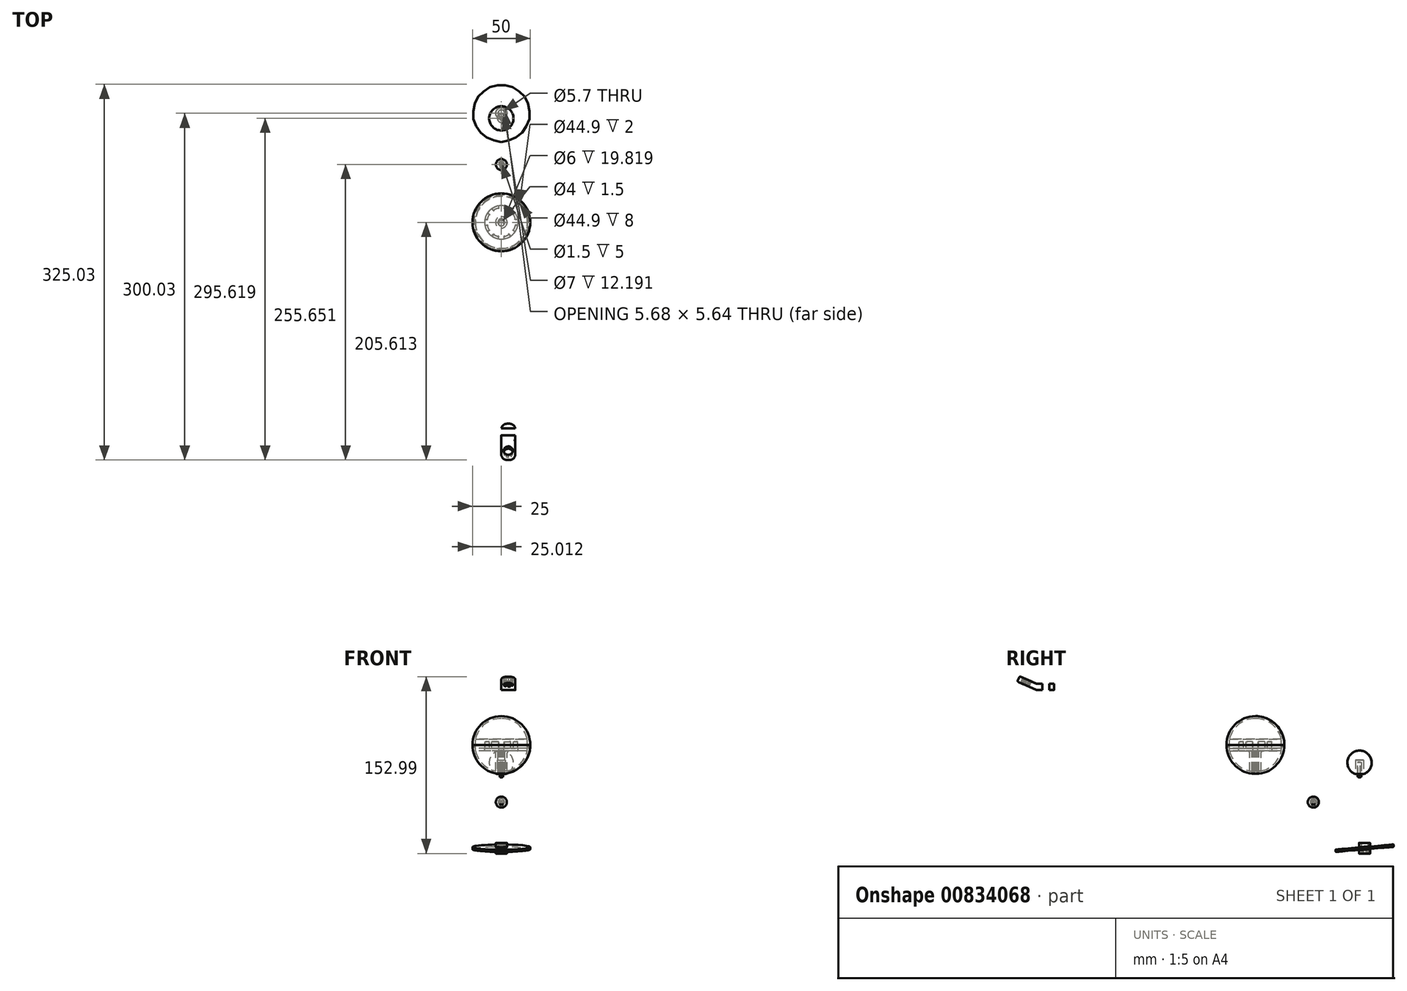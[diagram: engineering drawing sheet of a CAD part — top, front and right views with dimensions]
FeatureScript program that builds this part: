
annotation { "Feature Type Name" : "Feature", "Feature Type Description" : "" }
export const myFeature = defineFeature(function(context is Context, id is Id, definition is map)
    precondition{}
    {
        {
            var Q0;
            Q0=qCreatedBy(makeId("Right.planeOp"),FACE);
            var sketch = newSketch(context, id + "F0", { "sketchPlane" : qUnion([Q0])});
            skLineSegment(sketch, "E0", {"start": v(-206.61, 164.55) * mm, "end": v(-191.94, 158.17) * mm});
            skLineSegment(sketch, "E1", {"start": v(-191.94, 158.17) * mm, "end": v(-175.94, 158.17) * mm});
            skLineSegment(sketch, "E2", {"start": v(-206.61, 164.55) * mm, "end": v(-208.6, 159.96) * mm});
            skLineSegment(sketch, "E3", {"start": v(-208.6, 159.96) * mm, "end": v(-191.94, 152.71) * mm});
            skLineSegment(sketch, "E4", {"start": v(-191.94, 152.71) * mm, "end": v(-175.94, 152.71) * mm});
            skLineSegment(sketch, "E5", {"start": v(-175.94, 152.71) * mm, "end": v(-175.94, 158.17) * mm});
            skLineSegment(sketch, "E6.bottom", {"start": v(-186.94, 158.17) * mm, "end": v(-180.94, 158.17) * mm});
            skLineSegment(sketch, "E6.top", {"start": v(-186.94, 152.71) * mm, "end": v(-180.94, 152.71) * mm});
            skLineSegment(sketch, "E6.left", {"start": v(-186.94, 158.17) * mm, "end": v(-186.94, 152.71) * mm});
            skLineSegment(sketch, "E6.right", {"start": v(-180.94, 158.17) * mm, "end": v(-180.94, 152.71) * mm});
            skLineSegment(sketch, "E7", {"start": v(-202.94, 162.95) * mm, "end": v(-204.94, 158.37) * mm});
            skLineSegment(sketch, "E8", {"start": v(-195.6, 159.76) * mm, "end": v(-197.6, 155.18) * mm});
            skLineSegment(sketch, "E9", {"start": v(-199.28, 161.36) * mm, "end": v(-203.57, 151.48) * mm});
            skLineSegment(sketch, "E10", {"start": v(-199.28, 161.36) * mm, "end": v(-184, 196.48) * mm});
            skLineSegment(sketch, "E11", {"start": v(-183.94, 158.17) * mm, "end": v(-183.94, 142.94) * mm});
            skLineSegment(sketch, "E12", {"start": v(-183.94, 158.17) * mm, "end": v(-183.94, 196.54) * mm});
            skLineSegment(sketch, "E13", {"start": v(-200.94, 172.57) * mm, "end": v(-189.94, 167.78) * mm});
            skLineSegment(sketch, "E14", {"start": v(-189.94, 167.78) * mm, "end": v(-177.94, 167.78) * mm});
            skLineSegment(sketch, "E15", {"start": v(-298.35, 148.72) * mm, "end": v(-283.68, 142.34) * mm});
            skLineSegment(sketch, "E16", {"start": v(-283.68, 142.34) * mm, "end": v(-268.68, 142.34) * mm});
            skLineSegment(sketch, "E17", {"start": v(-298.35, 148.72) * mm, "end": v(-300.34, 144.14) * mm});
            skLineSegment(sketch, "E18", {"start": v(-300.34, 144.14) * mm, "end": v(-283.68, 136.9) * mm});
            skLineSegment(sketch, "E19", {"start": v(-283.68, 136.9) * mm, "end": v(-268.68, 136.9) * mm});
            skLineSegment(sketch, "E20", {"start": v(-268.68, 136.9) * mm, "end": v(-268.68, 142.34) * mm});
            skLineSegment(sketch, "E21.bottom", {"start": v(-278.68, 142.34) * mm, "end": v(-272.68, 142.34) * mm});
            skLineSegment(sketch, "E21.top", {"start": v(-278.68, 136.9) * mm, "end": v(-272.68, 136.9) * mm});
            skLineSegment(sketch, "E21.left", {"start": v(-278.68, 142.34) * mm, "end": v(-278.68, 136.9) * mm});
            skLineSegment(sketch, "E21.right", {"start": v(-272.68, 142.34) * mm, "end": v(-272.68, 136.9) * mm});
            skLineSegment(sketch, "E22", {"start": v(-294.68, 147.13) * mm, "end": v(-296.68, 142.54) * mm});
            skLineSegment(sketch, "E23", {"start": v(-287.35, 143.94) * mm, "end": v(-289.34, 139.35) * mm});
            skSolve(sketch);
        }
        {
            var Q0;
            {var subQ0=sQuery(id+"F0.wireOp",EDGE,"E17");Q0=makeQuery(id+"F0.imprint","IMPRINT",FACE,{"disambiguationData":[TD([[makeQuery(id+"F0.imprint","IMPRINT",EDGE,{"derivedFrom":subQ0}),1.0]])]});}
            var Q1;
            {var subQ3=sQuery(id+"F0.wireOp",EDGE,"E21.left");Q1=makeQuery(id+"F0.imprint","IMPRINT",FACE,{"disambiguationData":[TD([[makeQuery(id+"F0.imprint","IMPRINT",EDGE,{"derivedFrom":subQ3}),-1.0]])]});}
            var Q2;
            {var subQ0=sQuery(id+"F0.wireOp",EDGE,"E22");Q2=makeQuery(id+"F0.imprint","IMPRINT",FACE,{"disambiguationData":[TD([[makeQuery(id+"F0.imprint","IMPRINT",EDGE,{"derivedFrom":subQ0}),1.0]])]});}
            var Q3;
            Q3=makeQuery(id+"F0.imprint","IMPRINT",FACE,{"disambiguationData":[TD([[makeQuery(id+"F0.imprint","IMPRINT",EDGE,{"derivedFrom":sQuery(id+"F0.wireOp",EDGE,"E21.bottom")}),-1.0]])]});
            var Q4;
            {var subQ0=sQuery(id+"F0.wireOp",EDGE,"E20");Q4=makeQuery(id+"F0.imprint","IMPRINT",FACE,{"disambiguationData":[TD([[makeQuery(id+"F0.imprint","IMPRINT",EDGE,{"derivedFrom":subQ0}),1.0]])]});}
            extrude(context, id + "F1", {"entities" : qUnion([Q0, Q1, Q2, Q3, Q4]), "depth" : 12 * mm, "offsetDistance" : 25 * mm});
        }
        {
            var Q0;
            Q0=makeQuery(id+"F1.opExtrude","SWEPT_FACE",FACE,{"disambiguationData":[OSD([sQuery(id+"F0.wireOp",EDGE,"E15")])]});
            var sketch = newSketch(context, id + "F2", { "sketchPlane" : qUnion([Q0])});
            skArc(sketch, "E24", {"start": v(7.7, -322.29) * mm, "mid": v(6.7, -321.97) * mm, "end": v(5.66, -321.92) * mm});
            skArc(sketch, "E25", {"start": v(9.2, -323.68) * mm, "mid": v(8.52, -322.93) * mm, "end": v(7.66, -322.38) * mm});
            skLineSegment(sketch, "E26", {"start": v(7.66, -322.38) * mm, "end": v(7.7, -322.29) * mm});
            skLineSegment(sketch, "E27", {"start": v(9.2, -323.68) * mm, "end": v(9.28, -323.62) * mm});
            skArc(sketch, "E28.1.0", {"start": v(5.67, -322.02) * mm, "mid": v(4.68, -322.24) * mm, "end": v(3.77, -322.7) * mm});
            skLineSegment(sketch, "E28.1.1", {"start": v(3.77, -322.7) * mm, "end": v(3.71, -322.63) * mm});
            skLineSegment(sketch, "E28.1.2", {"start": v(5.67, -322.02) * mm, "end": v(5.66, -321.92) * mm});
            skArc(sketch, "E28.2.0", {"start": v(2.47, -324.25) * mm, "mid": v(2.16, -325.22) * mm, "end": v(2.11, -326.24) * mm});
            skLineSegment(sketch, "E28.2.1", {"start": v(2.11, -326.24) * mm, "end": v(2.01, -326.25) * mm});
            skLineSegment(sketch, "E28.2.2", {"start": v(2.47, -324.25) * mm, "end": v(2.38, -324.2) * mm});
            skArc(sketch, "E28.3.0", {"start": v(2.8, -328.14) * mm, "mid": v(3.48, -328.89) * mm, "end": v(4.34, -329.44) * mm});
            skLineSegment(sketch, "E28.3.1", {"start": v(4.34, -329.44) * mm, "end": v(4.3, -329.53) * mm});
            skLineSegment(sketch, "E28.3.2", {"start": v(2.8, -328.14) * mm, "end": v(2.72, -328.2) * mm});
            skArc(sketch, "E28.4.0", {"start": v(6.33, -329.8) * mm, "mid": v(7.32, -329.58) * mm, "end": v(8.23, -329.1) * mm});
            skLineSegment(sketch, "E28.4.1", {"start": v(8.23, -329.1) * mm, "end": v(8.29, -329.2) * mm});
            skLineSegment(sketch, "E28.4.2", {"start": v(6.33, -329.8) * mm, "end": v(6.34, -329.9) * mm});
            skArc(sketch, "E28.5.0", {"start": v(9.53, -327.57) * mm, "mid": v(9.84, -326.6) * mm, "end": v(9.89, -325.58) * mm});
            skLineSegment(sketch, "E28.5.1", {"start": v(9.89, -325.58) * mm, "end": v(9.99, -325.57) * mm});
            skLineSegment(sketch, "E28.5.2", {"start": v(9.53, -327.57) * mm, "end": v(9.62, -327.6) * mm});
            skArc(sketch, "E29.trimOffspring", {"start": v(3.71, -322.63) * mm, "mid": v(2.94, -323.33) * mm, "end": v(2.38, -324.2) * mm});
            skArc(sketch, "E30.trimOffspring", {"start": v(2.01, -326.25) * mm, "mid": v(2.24, -327.27) * mm, "end": v(2.72, -328.2) * mm});
            skArc(sketch, "E31.trimOffspring", {"start": v(9.99, -325.57) * mm, "mid": v(9.76, -324.55) * mm, "end": v(9.28, -323.62) * mm});
            skArc(sketch, "E32.trimOffspring", {"start": v(8.29, -329.2) * mm, "mid": v(9.06, -328.49) * mm, "end": v(9.62, -327.6) * mm});
            skArc(sketch, "E33.trimOffspring", {"start": v(4.3, -329.53) * mm, "mid": v(5.3, -329.85) * mm, "end": v(6.34, -329.9) * mm});
            skSolve(sketch);
        }
        {
            var Q0;
            Q0=makeQuery(id+"F1.opExtrude","SWEPT_FACE",FACE,{"disambiguationData":[OSD([sQuery(id+"F0.wireOp",EDGE,"E16"),sQuery(id+"F0.wireOp",EDGE,"E21.bottom")])]});
            var sketch = newSketch(context, id + "F3", { "sketchPlane" : qUnion([Q0])});
            skArc(sketch, "E34", {"start": v(7.34, -273) * mm, "mid": v(6.6, -272.74) * mm, "end": v(5.81, -272.68) * mm});
            skArc(sketch, "E35", {"start": v(8.38, -274.1) * mm, "mid": v(7.89, -273.54) * mm, "end": v(7.27, -273.13) * mm});
            skLineSegment(sketch, "E36", {"start": v(7.27, -273.13) * mm, "end": v(7.34, -273) * mm});
            skLineSegment(sketch, "E37", {"start": v(8.38, -274.1) * mm, "end": v(8.5, -274.02) * mm});
            skLineSegment(sketch, "E38.1.0", {"start": v(4.43, -273.3) * mm, "end": v(4.34, -273.18) * mm});
            skArc(sketch, "E38.1.1", {"start": v(5.82, -272.83) * mm, "mid": v(5.1, -272.98) * mm, "end": v(4.43, -273.3) * mm});
            skLineSegment(sketch, "E38.1.2", {"start": v(5.82, -272.83) * mm, "end": v(5.81, -272.68) * mm});
            skLineSegment(sketch, "E38.2.0", {"start": v(3.16, -275.85) * mm, "end": v(3, -275.86) * mm});
            skArc(sketch, "E38.2.1", {"start": v(3.45, -274.4) * mm, "mid": v(3.2, -275.11) * mm, "end": v(3.16, -275.85) * mm});
            skLineSegment(sketch, "E38.2.2", {"start": v(3.45, -274.4) * mm, "end": v(3.31, -274.34) * mm});
            skLineSegment(sketch, "E38.3.0", {"start": v(4.73, -278.23) * mm, "end": v(4.66, -278.36) * mm});
            skArc(sketch, "E38.3.1", {"start": v(3.62, -277.25) * mm, "mid": v(4.11, -277.81) * mm, "end": v(4.73, -278.23) * mm});
            skLineSegment(sketch, "E38.3.2", {"start": v(3.62, -277.25) * mm, "end": v(3.5, -277.33) * mm});
            skLineSegment(sketch, "E38.4.0", {"start": v(7.57, -278.05) * mm, "end": v(7.66, -278.18) * mm});
            skArc(sketch, "E38.4.1", {"start": v(6.18, -278.52) * mm, "mid": v(6.9, -278.38) * mm, "end": v(7.57, -278.05) * mm});
            skLineSegment(sketch, "E38.4.2", {"start": v(6.18, -278.52) * mm, "end": v(6.19, -278.67) * mm});
            skLineSegment(sketch, "E38.5.0", {"start": v(8.84, -275.5) * mm, "end": v(9, -275.5) * mm});
            skArc(sketch, "E38.5.1", {"start": v(8.55, -276.95) * mm, "mid": v(8.8, -276.24) * mm, "end": v(8.84, -275.5) * mm});
            skLineSegment(sketch, "E38.5.2", {"start": v(8.55, -276.95) * mm, "end": v(8.69, -277.01) * mm});
            skArc(sketch, "E39.trimOffspring", {"start": v(4.34, -273.18) * mm, "mid": v(3.75, -273.7) * mm, "end": v(3.31, -274.34) * mm});
            skArc(sketch, "E40.trimOffspring", {"start": v(3, -275.86) * mm, "mid": v(3.16, -276.63) * mm, "end": v(3.5, -277.33) * mm});
            skArc(sketch, "E41.trimOffspring", {"start": v(4.66, -278.36) * mm, "mid": v(5.4, -278.62) * mm, "end": v(6.19, -278.67) * mm});
            skArc(sketch, "E42.trimOffspring", {"start": v(7.66, -278.18) * mm, "mid": v(8.25, -277.66) * mm, "end": v(8.69, -277.01) * mm});
            skArc(sketch, "E43.trimOffspring", {"start": v(9, -275.5) * mm, "mid": v(8.84, -274.72) * mm, "end": v(8.5, -274.02) * mm});
            skSolve(sketch);
        }
        {
            var Q0;
            Q0=makeQuery(id+"F2.imprint","IMPRINT",FACE,{"disambiguationData":[TD([[makeQuery(id+"F2.imprint","IMPRINT",EDGE,{"derivedFrom":sQuery(id+"F2.wireOp",EDGE,"E24")}),1.0]])]});
            extrude(context, id + "F4", {"entities" : qUnion([Q0]), "operationType" : NewBodyOperationType.REMOVE, "oppositeDirection" : true, "depth" : 25 * mm, "offsetDistance" : 25 * mm});
        }
        {
            var Q0;
            Q0=makeQuery(id+"F3.imprint","IMPRINT",FACE,{"disambiguationData":[TD([[makeQuery(id+"F3.imprint","IMPRINT",EDGE,{"derivedFrom":sQuery(id+"F3.wireOp",EDGE,"E34")}),1.0]])]});
            extrude(context, id + "F5", {"entities" : qUnion([Q0]), "operationType" : NewBodyOperationType.REMOVE, "oppositeDirection" : true, "depth" : 25 * mm, "offsetDistance" : 25 * mm});
        }
        {
            var Q0;
            Q0=makeQuery(id+"F1.opExtrude","CAP_EDGE",EDGE,{"disambiguationData":[OSD([sQuery(id+"F0.wireOp",EDGE,"E17")])],"isStart":false});
            var Q1;
            Q1=makeQuery(id+"F1.opExtrude","CAP_EDGE",EDGE,{"disambiguationData":[OSD([sQuery(id+"F0.wireOp",EDGE,"E17")])],"isStart":true});
            var Q2;
            Q2=makeQuery(id+"F1.opExtrude","CAP_EDGE",EDGE,{"disambiguationData":[OSD([sQuery(id+"F0.wireOp",EDGE,"E20")])],"isStart":false});
            var Q3;
            Q3=makeQuery(id+"F1.opExtrude","CAP_EDGE",EDGE,{"disambiguationData":[OSD([sQuery(id+"F0.wireOp",EDGE,"E20")])],"isStart":true});
            fillet(context, id + "F6", {"entities" : qUnion([Q0, Q1, Q2, Q3]), "radius" : 5 * mm, "tangentPropagation" : true, "allowEdgeOverflow" : false});
        }
        {
            var Q0;
            Q0=makeQuery(id+"F1.opExtrude","CAP_EDGE",EDGE,{"disambiguationData":[OSD([sQuery(id+"F0.wireOp",EDGE,"E15")])],"isStart":false});
            var Q1;
            Q1=makeQuery(id+"F6.opFillet","BLEND_EDGE",EDGE,{"blendedFrom":[makeQuery(id+"F1.opExtrude","CAP_EDGE",EDGE,{"disambiguationData":[OSD([sQuery(id+"F0.wireOp",EDGE,"E17")])],"isStart":false}),makeQuery(id+"F1.opExtrude","SWEPT_FACE",FACE,{"disambiguationData":[OSD([sQuery(id+"F0.wireOp",EDGE,"E15")])]})],"blendedInto":[makeQuery(id+"F1.opExtrude","SWEPT_FACE",FACE,{"disambiguationData":[OSD([sQuery(id+"F0.wireOp",EDGE,"E15")])]})]});
            var Q2;
            Q2=makeQuery(id+"F1.opExtrude","CAP_EDGE",EDGE,{"disambiguationData":[OSD([sQuery(id+"F0.wireOp",EDGE,"E16"),sQuery(id+"F0.wireOp",EDGE,"E21.bottom")])],"isStart":true});
            var Q3;
            Q3=makeQuery(id+"F1.opExtrude","CAP_EDGE",EDGE,{"disambiguationData":[OSD([sQuery(id+"F0.wireOp",EDGE,"E18")])],"isStart":false});
            var Q4;
            Q4=makeQuery(id+"F1.opExtrude","CAP_EDGE",EDGE,{"disambiguationData":[OSD([sQuery(id+"F0.wireOp",EDGE,"E19"),sQuery(id+"F0.wireOp",EDGE,"E21.top")])],"isStart":true});
            var Q5;
            Q5=makeQuery(id+"F1.opExtrude","SWEPT_EDGE",EDGE,{"disambiguationData":[OSD([sQuery(id+"F0.wireOp",EDGE,"E18"),sQuery(id+"F0.wireOp",EDGE,"E19")])]});
            var Q6;
            Q6=makeQuery(id+"F1.opExtrude","SWEPT_EDGE",EDGE,{"disambiguationData":[OSD([sQuery(id+"F0.wireOp",EDGE,"E15"),sQuery(id+"F0.wireOp",EDGE,"E16")])]});
            fillet(context, id + "F7", {"entities" : qUnion([Q0, Q1, Q2, Q3, Q4, Q5, Q6]), "radius" : 1 * mm, "tangentPropagation" : true, "allowEdgeOverflow" : false});
        }
        {
            var Q0;
            Q0=qCreatedBy(makeId("Right.planeOp"),FACE);
            var sketch = newSketch(context, id + "F8", { "sketchPlane" : qUnion([Q0])});
            skArc(sketch, "E44", {"start": v(-94.42, 114.27) * mm, "mid": v(-119.37, 90.78) * mm, "end": v(-97.42, 64.45) * mm});
            skLineSegment(sketch, "E45.right", {"start": v(-97.42, 64.45) * mm, "end": v(-97.42, 84.27) * mm});
            skPoint(sketch, "E46.orphan", {"position": v(-97.42, 61.17) * mm});
            skPoint(sketch, "E47.orphan", {"position": v(-91.42, 61.17) * mm});
            skPoint(sketch, "E48.left.end.orphan", {"position": v(-71.97, 94.27) * mm});
            skPoint(sketch, "E49.orphan", {"position": v(-91.42, 117.38) * mm});
            skPoint(sketch, "E50.orphan", {"position": v(-97.42, 117.38) * mm});
            skPoint(sketch, "E48.right.end.orphan", {"position": v(-116.87, 94.27) * mm});
            skPoint(sketch, "E48.right.start.orphan", {"position": v(-116.87, 84.27) * mm});
            skLineSegment(sketch, "E51", {"start": v(-96.92, 86.27) * mm, "end": v(-106.37, 86.27) * mm});
            skLineSegment(sketch, "E52", {"start": v(-96.42, 85.77) * mm, "end": v(-96.42, 84.27) * mm});
            skLineSegment(sketch, "E53", {"start": v(-108.37, 84.27) * mm, "end": v(-101.42, 84.27) * mm});
            skLineSegment(sketch, "E54", {"start": v(-99.42, 82.27) * mm, "end": v(-99.42, 66.82) * mm});
            skLineSegment(sketch, "E55.top", {"start": v(-108.87, 92.27) * mm, "end": v(-106.87, 92.27) * mm});
            skLineSegment(sketch, "E55.left", {"start": v(-108.87, 86.27) * mm, "end": v(-108.87, 92.27) * mm});
            skLineSegment(sketch, "E55.right", {"start": v(-106.87, 86.77) * mm, "end": v(-106.87, 92.27) * mm});
            skArc(sketch, "E56.trimOffspring", {"start": v(-116.87, 84.27) * mm, "mid": v(-110.68, 73) * mm, "end": v(-99.42, 66.82) * mm});
            skLineSegment(sketch, "E57.trimOffspring", {"start": v(-116.87, 86.27) * mm, "end": v(-117.22, 86.27) * mm});
            skLineSegment(sketch, "E58.trimOffspring", {"start": v(-96.42, 84.27) * mm, "end": v(-97.42, 84.27) * mm});
            skLineSegment(sketch, "E59", {"start": v(-116.87, 94.27) * mm, "end": v(-116.87, 86.27) * mm});
            skLineSegment(sketch, "E60", {"start": v(-119.42, 89.27) * mm, "end": v(-118.14, 89.27) * mm});
            skPoint(sketch, "E60.startSnap0", {"position": v(-116.87, 89.27) * mm});
            skLineSegment(sketch, "E61", {"start": v(-118.14, 89.27) * mm, "end": v(-117.22, 86.27) * mm});
            skLineSegment(sketch, "E62", {"start": v(-94.42, 112.27) * mm, "end": v(-94.42, 114.27) * mm});
            skArc(sketch, "E63.trimOffspring", {"start": v(-94.42, 112.27) * mm, "mid": v(-108.8, 107.22) * mm, "end": v(-116.87, 94.27) * mm});
            skPoint(sketch, "E48.bottom.start.orphan", {"position": v(-71.97, 84.27) * mm});
            skLineSegment(sketch, "E64", {"start": v(-94.42, 89.27) * mm, "end": v(-94.42, 76.17) * mm});
            skLineSegment(sketch, "E65", {"start": v(-108.87, 86.27) * mm, "end": v(-108.87, 84.77) * mm});
            skLineSegment(sketch, "E66", {"start": v(-116.87, 84.27) * mm, "end": v(-116.87, 86.27) * mm});
            skPoint(sketch, "E67.visualSharp", {"position": v(-106.87, 86.27) * mm});
            skArc(sketch, "E67.filletArc", {"start": v(-106.87, 86.77) * mm, "mid": v(-106.72, 86.42) * mm, "end": v(-106.37, 86.27) * mm});
            skPoint(sketch, "E68.visualSharp", {"position": v(-108.87, 84.27) * mm});
            skArc(sketch, "E68.filletArc", {"start": v(-108.87, 84.77) * mm, "mid": v(-108.72, 84.42) * mm, "end": v(-108.37, 84.27) * mm});
            skPoint(sketch, "E69.visualSharp", {"position": v(-99.42, 84.27) * mm});
            skArc(sketch, "E69.filletArc", {"start": v(-99.42, 82.27) * mm, "mid": v(-100, 83.69) * mm, "end": v(-101.42, 84.27) * mm});
            skPoint(sketch, "E70.visualSharp", {"position": v(-96.42, 86.27) * mm});
            skArc(sketch, "E70.filletArc", {"start": v(-96.42, 85.77) * mm, "mid": v(-96.56, 86.13) * mm, "end": v(-96.92, 86.27) * mm});
            skSolve(sketch);
        }
        {
            var Q0;
            {var subQ1=sQuery(id+"F8.wireOp",EDGE,"E45.right");Q0=makeQuery(id+"F8.imprint","IMPRINT",FACE,{"disambiguationData":[TD([[makeQuery(id+"F8.imprint","IMPRINT",EDGE,{"derivedFrom":subQ1}),1.0]])]});}
            var Q1;
            Q1=sQuery(id+"F8.wireOp",EDGE,"E64");
            revolve(context, id + "F9", {"surfaceOperationType" : NewSurfaceOperationType.NEW, "entities" : qUnion([Q0]), "axis" : qUnion([Q1]), "revolveType" : RevolveType.FULL});
        }
        {
            var Q0;
            {var subQ0=sQuery(id+"F8.wireOp",EDGE,"E59");Q0=makeQuery(id+"F8.imprint","IMPRINT",FACE,{"disambiguationData":[TD([[makeQuery(id+"F8.imprint","IMPRINT",EDGE,{"derivedFrom":subQ0}),-1.0]])]});}
            var Q1;
            Q1=sQuery(id+"F8.wireOp",EDGE,"E64");
            revolve(context, id + "F10", {"surfaceOperationType" : NewSurfaceOperationType.NEW, "entities" : qUnion([Q0]), "axis" : qUnion([Q1]), "revolveType" : RevolveType.FULL});
        }
        {
            var Q0;
            Q0=makeQuery(id+"F9.opRevolve","SWEPT_FACE",FACE,{"disambiguationData":[OSD([sQuery(id+"F8.wireOp",EDGE,"E55.top")])]});
            var sketch = newSketch(context, id + "F11", { "sketchPlane" : qUnion([Q0])});
            skArc(sketch, "E71", {"start": v(2.4, -79.89) * mm, "mid": v(0, -79.7) * mm, "end": v(-2.4, -79.89) * mm});
            skArc(sketch, "E72", {"start": v(2.4, -83.2) * mm, "mid": v(0, -82.95) * mm, "end": v(-2.4, -83.2) * mm});
            skLineSegment(sketch, "E73", {"start": v(-2.4, -79.89) * mm, "end": v(-2.4, -83.2) * mm});
            skLineSegment(sketch, "E74", {"start": v(2.4, -79.89) * mm, "end": v(2.4, -83.2) * mm});
            skArc(sketch, "E75.1.0", {"start": v(-8.58, -82.45) * mm, "mid": v(-10.41, -84) * mm, "end": v(-11.97, -85.84) * mm});
            skLineSegment(sketch, "E75.1.1", {"start": v(-8.58, -82.45) * mm, "end": v(-6.24, -84.79) * mm});
            skLineSegment(sketch, "E75.1.2", {"start": v(-11.97, -85.84) * mm, "end": v(-9.63, -88.18) * mm});
            skArc(sketch, "E75.1.3", {"start": v(-6.24, -84.79) * mm, "mid": v(-8.11, -86.3) * mm, "end": v(-9.63, -88.18) * mm});
            skArc(sketch, "E75.2.0", {"start": v(-14.53, -92.02) * mm, "mid": v(-14.73, -94.42) * mm, "end": v(-14.53, -96.82) * mm});
            skLineSegment(sketch, "E75.2.1", {"start": v(-14.53, -92.02) * mm, "end": v(-11.22, -92.02) * mm});
            skLineSegment(sketch, "E75.2.2", {"start": v(-14.53, -96.82) * mm, "end": v(-11.22, -96.82) * mm});
            skArc(sketch, "E75.2.3", {"start": v(-11.22, -92.02) * mm, "mid": v(-11.47, -94.42) * mm, "end": v(-11.22, -96.82) * mm});
            skArc(sketch, "E75.3.0", {"start": v(-11.97, -103) * mm, "mid": v(-10.41, -104.83) * mm, "end": v(-8.58, -106.39) * mm});
            skLineSegment(sketch, "E75.3.1", {"start": v(-11.97, -103) * mm, "end": v(-9.63, -100.65) * mm});
            skLineSegment(sketch, "E75.3.2", {"start": v(-8.58, -106.39) * mm, "end": v(-6.24, -104.05) * mm});
            skArc(sketch, "E75.3.3", {"start": v(-9.63, -100.65) * mm, "mid": v(-8.11, -102.53) * mm, "end": v(-6.24, -104.05) * mm});
            skArc(sketch, "E75.4.0", {"start": v(-2.4, -108.95) * mm, "mid": v(0, -109.14) * mm, "end": v(2.4, -108.95) * mm});
            skLineSegment(sketch, "E75.4.1", {"start": v(-2.4, -108.95) * mm, "end": v(-2.4, -105.64) * mm});
            skLineSegment(sketch, "E75.4.2", {"start": v(2.4, -108.95) * mm, "end": v(2.4, -105.64) * mm});
            skArc(sketch, "E75.4.3", {"start": v(-2.4, -105.64) * mm, "mid": v(0, -105.89) * mm, "end": v(2.4, -105.64) * mm});
            skArc(sketch, "E75.5.0", {"start": v(8.58, -106.39) * mm, "mid": v(10.41, -104.83) * mm, "end": v(11.97, -103) * mm});
            skLineSegment(sketch, "E75.5.1", {"start": v(8.58, -106.39) * mm, "end": v(6.24, -104.05) * mm});
            skLineSegment(sketch, "E75.5.2", {"start": v(11.97, -103) * mm, "end": v(9.63, -100.65) * mm});
            skArc(sketch, "E75.5.3", {"start": v(6.24, -104.05) * mm, "mid": v(8.11, -102.53) * mm, "end": v(9.63, -100.65) * mm});
            skArc(sketch, "E75.6.0", {"start": v(14.53, -96.82) * mm, "mid": v(14.73, -94.42) * mm, "end": v(14.53, -92.02) * mm});
            skLineSegment(sketch, "E75.6.1", {"start": v(14.53, -96.82) * mm, "end": v(11.22, -96.82) * mm});
            skLineSegment(sketch, "E75.6.2", {"start": v(14.53, -92.02) * mm, "end": v(11.22, -92.02) * mm});
            skArc(sketch, "E75.6.3", {"start": v(11.22, -96.82) * mm, "mid": v(11.47, -94.42) * mm, "end": v(11.22, -92.02) * mm});
            skArc(sketch, "E75.7.0", {"start": v(11.97, -85.84) * mm, "mid": v(10.41, -84) * mm, "end": v(8.58, -82.45) * mm});
            skLineSegment(sketch, "E75.7.1", {"start": v(11.97, -85.84) * mm, "end": v(9.63, -88.18) * mm});
            skLineSegment(sketch, "E75.7.2", {"start": v(8.58, -82.45) * mm, "end": v(6.24, -84.79) * mm});
            skArc(sketch, "E75.7.3", {"start": v(9.63, -88.18) * mm, "mid": v(8.11, -86.3) * mm, "end": v(6.24, -84.79) * mm});
            skSolve(sketch);
        }
        {
            var Q0;
            Q0 = qSketchRegion(id + "F11", true);
            extrude(context, id + "F12", {"entities" : qUnion([Q0]), "operationType" : NewBodyOperationType.REMOVE, "oppositeDirection" : true, "depth" : 6 * mm, "offsetDistance" : 25 * mm});
        }
        {
            var Q0;
            {var subQ0=sQuery(id+"F8.wireOp",EDGE,"E55.top");var subQ1=sQuery(id+"F8.wireOp",EDGE,"E55.left");Q0=makeQuery(id+"F12.boolean.opBoolean","SPLIT",EDGE,{"disambiguationData":[TD([makeQuery(id+"F12.opExtrude","SWEPT_FACE",FACE,{"disambiguationData":[OSD([sQuery(id+"F11.wireOp",EDGE,"E75.3.2")])]})])],"derivedFrom":makeQuery(id+"F9.opRevolve","SWEPT_EDGE",EDGE,{"disambiguationData":[OSD([subQ0,subQ1])]})});}
            var Q1;
            Q1=makeQuery(id+"F12.boolean.opBoolean","COPY",EDGE,{"derivedFrom":makeQuery(id+"F12.opExtrude","CAP_EDGE",EDGE,{"disambiguationData":[OSD([sQuery(id+"F11.wireOp",EDGE,"E75.4.1")])],"isStart":true})});
            var Q2;
            {var subQ0=sQuery(id+"F8.wireOp",EDGE,"E55.top");var subQ1=sQuery(id+"F8.wireOp",EDGE,"E55.right");Q2=makeQuery(id+"F12.boolean.opBoolean","SPLIT",EDGE,{"disambiguationData":[TD([makeQuery(id+"F12.opExtrude","SWEPT_FACE",FACE,{"disambiguationData":[OSD([sQuery(id+"F11.wireOp",EDGE,"E75.3.2")])]})])],"derivedFrom":makeQuery(id+"F9.opRevolve","SWEPT_EDGE",EDGE,{"disambiguationData":[OSD([subQ0,subQ1])]})});}
            var Q3;
            Q3=makeQuery(id+"F12.boolean.opBoolean","COPY",EDGE,{"derivedFrom":makeQuery(id+"F12.opExtrude","CAP_EDGE",EDGE,{"disambiguationData":[OSD([sQuery(id+"F11.wireOp",EDGE,"E75.3.2")])],"isStart":true})});
            var Q4;
            Q4=makeQuery(id+"F12.boolean.opBoolean","COPY",EDGE,{"derivedFrom":makeQuery(id+"F12.opExtrude","CAP_EDGE",EDGE,{"disambiguationData":[OSD([sQuery(id+"F11.wireOp",EDGE,"E75.3.1")])],"isStart":true})});
            var Q5;
            {var subQ0=sQuery(id+"F8.wireOp",EDGE,"E55.top");var subQ1=sQuery(id+"F8.wireOp",EDGE,"E55.left");Q5=makeQuery(id+"F12.boolean.opBoolean","SPLIT",EDGE,{"disambiguationData":[TD([makeQuery(id+"F12.opExtrude","SWEPT_FACE",FACE,{"disambiguationData":[OSD([sQuery(id+"F11.wireOp",EDGE,"E75.2.2")])]})])],"derivedFrom":makeQuery(id+"F9.opRevolve","SWEPT_EDGE",EDGE,{"disambiguationData":[OSD([subQ0,subQ1])]})});}
            var Q6;
            {var subQ0=sQuery(id+"F8.wireOp",EDGE,"E55.top");var subQ1=sQuery(id+"F8.wireOp",EDGE,"E55.right");Q6=makeQuery(id+"F12.boolean.opBoolean","SPLIT",EDGE,{"disambiguationData":[TD([makeQuery(id+"F12.opExtrude","SWEPT_FACE",FACE,{"disambiguationData":[OSD([sQuery(id+"F11.wireOp",EDGE,"E75.2.2")])]})])],"derivedFrom":makeQuery(id+"F9.opRevolve","SWEPT_EDGE",EDGE,{"disambiguationData":[OSD([subQ0,subQ1])]})});}
            var Q7;
            Q7=makeQuery(id+"F12.boolean.opBoolean","COPY",EDGE,{"derivedFrom":makeQuery(id+"F12.opExtrude","CAP_EDGE",EDGE,{"disambiguationData":[OSD([sQuery(id+"F11.wireOp",EDGE,"E75.2.2")])],"isStart":true})});
            var Q8;
            Q8=makeQuery(id+"F12.boolean.opBoolean","COPY",EDGE,{"derivedFrom":makeQuery(id+"F12.opExtrude","CAP_EDGE",EDGE,{"disambiguationData":[OSD([sQuery(id+"F11.wireOp",EDGE,"E75.2.1")])],"isStart":true})});
            var Q9;
            {var subQ0=sQuery(id+"F8.wireOp",EDGE,"E55.top");var subQ1=sQuery(id+"F8.wireOp",EDGE,"E55.left");Q9=makeQuery(id+"F12.boolean.opBoolean","SPLIT",EDGE,{"disambiguationData":[TD([makeQuery(id+"F12.opExtrude","SWEPT_FACE",FACE,{"disambiguationData":[OSD([sQuery(id+"F11.wireOp",EDGE,"E75.1.2")])]})])],"derivedFrom":makeQuery(id+"F9.opRevolve","SWEPT_EDGE",EDGE,{"disambiguationData":[OSD([subQ0,subQ1])]})});}
            var Q10;
            Q10=makeQuery(id+"F12.boolean.opBoolean","COPY",EDGE,{"derivedFrom":makeQuery(id+"F12.opExtrude","CAP_EDGE",EDGE,{"disambiguationData":[OSD([sQuery(id+"F11.wireOp",EDGE,"E75.1.2")])],"isStart":true})});
            var Q11;
            {var subQ0=sQuery(id+"F8.wireOp",EDGE,"E55.top");var subQ1=sQuery(id+"F8.wireOp",EDGE,"E55.right");Q11=makeQuery(id+"F12.boolean.opBoolean","SPLIT",EDGE,{"disambiguationData":[TD([makeQuery(id+"F12.opExtrude","SWEPT_FACE",FACE,{"disambiguationData":[OSD([sQuery(id+"F11.wireOp",EDGE,"E75.1.2")])]})])],"derivedFrom":makeQuery(id+"F9.opRevolve","SWEPT_EDGE",EDGE,{"disambiguationData":[OSD([subQ0,subQ1])]})});}
            var Q12;
            {var subQ0=sQuery(id+"F8.wireOp",EDGE,"E55.top");var subQ1=sQuery(id+"F8.wireOp",EDGE,"E55.right");Q12=makeQuery(id+"F12.boolean.opBoolean","SPLIT",EDGE,{"disambiguationData":[TD([makeQuery(id+"F12.opExtrude","SWEPT_FACE",FACE,{"disambiguationData":[OSD([sQuery(id+"F11.wireOp",EDGE,"E73")])]})])],"derivedFrom":makeQuery(id+"F9.opRevolve","SWEPT_EDGE",EDGE,{"disambiguationData":[OSD([subQ0,subQ1])]})});}
            var Q13;
            Q13=makeQuery(id+"F12.boolean.opBoolean","COPY",EDGE,{"derivedFrom":makeQuery(id+"F12.opExtrude","CAP_EDGE",EDGE,{"disambiguationData":[OSD([sQuery(id+"F11.wireOp",EDGE,"E75.1.1")])],"isStart":true})});
            var Q14;
            {var subQ0=sQuery(id+"F8.wireOp",EDGE,"E55.top");var subQ1=sQuery(id+"F8.wireOp",EDGE,"E55.left");Q14=makeQuery(id+"F12.boolean.opBoolean","SPLIT",EDGE,{"disambiguationData":[TD([makeQuery(id+"F12.opExtrude","SWEPT_FACE",FACE,{"disambiguationData":[OSD([sQuery(id+"F11.wireOp",EDGE,"E73")])]})])],"derivedFrom":makeQuery(id+"F9.opRevolve","SWEPT_EDGE",EDGE,{"disambiguationData":[OSD([subQ0,subQ1])]})});}
            var Q15;
            Q15=makeQuery(id+"F12.boolean.opBoolean","COPY",EDGE,{"derivedFrom":makeQuery(id+"F12.opExtrude","CAP_EDGE",EDGE,{"disambiguationData":[OSD([sQuery(id+"F11.wireOp",EDGE,"E73")])],"isStart":true})});
            var Q16;
            Q16=makeQuery(id+"F12.boolean.opBoolean","COPY",EDGE,{"derivedFrom":makeQuery(id+"F12.opExtrude","CAP_EDGE",EDGE,{"disambiguationData":[OSD([sQuery(id+"F11.wireOp",EDGE,"E74")])],"isStart":true})});
            var Q17;
            {var subQ0=sQuery(id+"F8.wireOp",EDGE,"E55.top");var subQ1=sQuery(id+"F8.wireOp",EDGE,"E55.right");Q17=makeQuery(id+"F12.boolean.opBoolean","SPLIT",EDGE,{"disambiguationData":[TD([makeQuery(id+"F12.opExtrude","SWEPT_FACE",FACE,{"disambiguationData":[OSD([sQuery(id+"F11.wireOp",EDGE,"E74")])]})])],"derivedFrom":makeQuery(id+"F9.opRevolve","SWEPT_EDGE",EDGE,{"disambiguationData":[OSD([subQ0,subQ1])]})});}
            var Q18;
            {var subQ0=sQuery(id+"F8.wireOp",EDGE,"E55.top");var subQ1=sQuery(id+"F8.wireOp",EDGE,"E55.left");Q18=makeQuery(id+"F12.boolean.opBoolean","SPLIT",EDGE,{"disambiguationData":[TD([makeQuery(id+"F12.opExtrude","SWEPT_FACE",FACE,{"disambiguationData":[OSD([sQuery(id+"F11.wireOp",EDGE,"E74")])]})])],"derivedFrom":makeQuery(id+"F9.opRevolve","SWEPT_EDGE",EDGE,{"disambiguationData":[OSD([subQ0,subQ1])]})});}
            var Q19;
            Q19=makeQuery(id+"F12.boolean.opBoolean","COPY",EDGE,{"derivedFrom":makeQuery(id+"F12.opExtrude","CAP_EDGE",EDGE,{"disambiguationData":[OSD([sQuery(id+"F11.wireOp",EDGE,"E75.7.2")])],"isStart":true})});
            var Q20;
            Q20=makeQuery(id+"F12.boolean.opBoolean","COPY",EDGE,{"derivedFrom":makeQuery(id+"F12.opExtrude","CAP_EDGE",EDGE,{"disambiguationData":[OSD([sQuery(id+"F11.wireOp",EDGE,"E75.7.1")])],"isStart":true})});
            var Q21;
            {var subQ0=sQuery(id+"F8.wireOp",EDGE,"E55.top");var subQ1=sQuery(id+"F8.wireOp",EDGE,"E55.right");Q21=makeQuery(id+"F12.boolean.opBoolean","SPLIT",EDGE,{"disambiguationData":[TD([makeQuery(id+"F12.opExtrude","SWEPT_FACE",FACE,{"disambiguationData":[OSD([sQuery(id+"F11.wireOp",EDGE,"E75.6.2")])]})])],"derivedFrom":makeQuery(id+"F9.opRevolve","SWEPT_EDGE",EDGE,{"disambiguationData":[OSD([subQ0,subQ1])]})});}
            var Q22;
            {var subQ0=sQuery(id+"F8.wireOp",EDGE,"E55.top");var subQ1=sQuery(id+"F8.wireOp",EDGE,"E55.left");Q22=makeQuery(id+"F12.boolean.opBoolean","SPLIT",EDGE,{"disambiguationData":[TD([makeQuery(id+"F12.opExtrude","SWEPT_FACE",FACE,{"disambiguationData":[OSD([sQuery(id+"F11.wireOp",EDGE,"E75.6.2")])]})])],"derivedFrom":makeQuery(id+"F9.opRevolve","SWEPT_EDGE",EDGE,{"disambiguationData":[OSD([subQ0,subQ1])]})});}
            var Q23;
            Q23=makeQuery(id+"F12.boolean.opBoolean","COPY",EDGE,{"derivedFrom":makeQuery(id+"F12.opExtrude","CAP_EDGE",EDGE,{"disambiguationData":[OSD([sQuery(id+"F11.wireOp",EDGE,"E75.6.2")])],"isStart":true})});
            var Q24;
            Q24=makeQuery(id+"F12.boolean.opBoolean","COPY",EDGE,{"derivedFrom":makeQuery(id+"F12.opExtrude","CAP_EDGE",EDGE,{"disambiguationData":[OSD([sQuery(id+"F11.wireOp",EDGE,"E75.6.1")])],"isStart":true})});
            var Q25;
            {var subQ0=sQuery(id+"F8.wireOp",EDGE,"E55.top");var subQ1=sQuery(id+"F8.wireOp",EDGE,"E55.left");Q25=makeQuery(id+"F12.boolean.opBoolean","SPLIT",EDGE,{"disambiguationData":[TD([makeQuery(id+"F12.opExtrude","SWEPT_FACE",FACE,{"disambiguationData":[OSD([sQuery(id+"F11.wireOp",EDGE,"E75.5.2")])]})])],"derivedFrom":makeQuery(id+"F9.opRevolve","SWEPT_EDGE",EDGE,{"disambiguationData":[OSD([subQ0,subQ1])]})});}
            var Q26;
            {var subQ0=sQuery(id+"F8.wireOp",EDGE,"E55.top");var subQ1=sQuery(id+"F8.wireOp",EDGE,"E55.right");Q26=makeQuery(id+"F12.boolean.opBoolean","SPLIT",EDGE,{"disambiguationData":[TD([makeQuery(id+"F12.opExtrude","SWEPT_FACE",FACE,{"disambiguationData":[OSD([sQuery(id+"F11.wireOp",EDGE,"E75.5.2")])]})])],"derivedFrom":makeQuery(id+"F9.opRevolve","SWEPT_EDGE",EDGE,{"disambiguationData":[OSD([subQ0,subQ1])]})});}
            var Q27;
            Q27=makeQuery(id+"F12.boolean.opBoolean","COPY",EDGE,{"derivedFrom":makeQuery(id+"F12.opExtrude","CAP_EDGE",EDGE,{"disambiguationData":[OSD([sQuery(id+"F11.wireOp",EDGE,"E75.5.2")])],"isStart":true})});
            var Q28;
            Q28=makeQuery(id+"F12.boolean.opBoolean","COPY",EDGE,{"derivedFrom":makeQuery(id+"F12.opExtrude","CAP_EDGE",EDGE,{"disambiguationData":[OSD([sQuery(id+"F11.wireOp",EDGE,"E75.5.1")])],"isStart":true})});
            var Q29;
            {var subQ0=sQuery(id+"F8.wireOp",EDGE,"E55.top");var subQ1=sQuery(id+"F8.wireOp",EDGE,"E55.left");Q29=makeQuery(id+"F12.boolean.opBoolean","SPLIT",EDGE,{"disambiguationData":[TD([makeQuery(id+"F12.opExtrude","SWEPT_FACE",FACE,{"disambiguationData":[OSD([sQuery(id+"F11.wireOp",EDGE,"E75.4.2")])]})])],"derivedFrom":makeQuery(id+"F9.opRevolve","SWEPT_EDGE",EDGE,{"disambiguationData":[OSD([subQ0,subQ1])]})});}
            var Q30;
            {var subQ0=sQuery(id+"F8.wireOp",EDGE,"E55.top");var subQ1=sQuery(id+"F8.wireOp",EDGE,"E55.right");Q30=makeQuery(id+"F12.boolean.opBoolean","SPLIT",EDGE,{"disambiguationData":[TD([makeQuery(id+"F12.opExtrude","SWEPT_FACE",FACE,{"disambiguationData":[OSD([sQuery(id+"F11.wireOp",EDGE,"E75.4.2")])]})])],"derivedFrom":makeQuery(id+"F9.opRevolve","SWEPT_EDGE",EDGE,{"disambiguationData":[OSD([subQ0,subQ1])]})});}
            var Q31;
            Q31=makeQuery(id+"F12.boolean.opBoolean","COPY",EDGE,{"derivedFrom":makeQuery(id+"F12.opExtrude","CAP_EDGE",EDGE,{"disambiguationData":[OSD([sQuery(id+"F11.wireOp",EDGE,"E75.4.2")])],"isStart":true})});
            fillet(context, id + "F13", {"entities" : qUnion([Q0, Q1, Q2, Q3, Q4, Q5, Q6, Q7, Q8, Q9, Q10, Q11, Q12, Q13, Q14, Q15, Q16, Q17, Q18, Q19, Q20, Q21, Q22, Q23, Q24, Q25, Q26, Q27, Q28, Q29, Q30, Q31]), "radius" : 0.5 * mm, "tangentPropagation" : true, "allowEdgeOverflow" : false});
        }
        {
            var Q0;
            Q0=makeQuery(id+"F12.boolean.opBoolean","INTERSECT",EDGE,{"derivedFrom":[makeQuery(id+"F9.opRevolve","SWEPT_FACE",FACE,{"disambiguationData":[OSD([sQuery(id+"F8.wireOp",EDGE,"E55.left")])]}),makeQuery(id+"F12.opExtrude","SWEPT_FACE",FACE,{"disambiguationData":[OSD([sQuery(id+"F11.wireOp",EDGE,"E75.6.1")])]})]});
            var Q1;
            Q1=makeQuery(id+"F12.boolean.opBoolean","INTERSECT",EDGE,{"derivedFrom":[makeQuery(id+"F9.opRevolve","SWEPT_FACE",FACE,{"disambiguationData":[OSD([sQuery(id+"F8.wireOp",EDGE,"E55.right")])]}),makeQuery(id+"F12.opExtrude","SWEPT_FACE",FACE,{"disambiguationData":[OSD([sQuery(id+"F11.wireOp",EDGE,"E75.6.1")])]})]});
            var Q2;
            Q2=makeQuery(id+"F12.boolean.opBoolean","INTERSECT",EDGE,{"derivedFrom":[makeQuery(id+"F9.opRevolve","SWEPT_FACE",FACE,{"disambiguationData":[OSD([sQuery(id+"F8.wireOp",EDGE,"E55.left")])]}),makeQuery(id+"F12.opExtrude","SWEPT_FACE",FACE,{"disambiguationData":[OSD([sQuery(id+"F11.wireOp",EDGE,"E75.6.2")])]})]});
            var Q3;
            Q3=makeQuery(id+"F12.boolean.opBoolean","INTERSECT",EDGE,{"derivedFrom":[makeQuery(id+"F9.opRevolve","SWEPT_FACE",FACE,{"disambiguationData":[OSD([sQuery(id+"F8.wireOp",EDGE,"E55.left")])]}),makeQuery(id+"F12.opExtrude","SWEPT_FACE",FACE,{"disambiguationData":[OSD([sQuery(id+"F11.wireOp",EDGE,"E75.7.1")])]})]});
            var Q4;
            Q4=makeQuery(id+"F12.boolean.opBoolean","INTERSECT",EDGE,{"derivedFrom":[makeQuery(id+"F9.opRevolve","SWEPT_FACE",FACE,{"disambiguationData":[OSD([sQuery(id+"F8.wireOp",EDGE,"E55.right")])]}),makeQuery(id+"F12.opExtrude","SWEPT_FACE",FACE,{"disambiguationData":[OSD([sQuery(id+"F11.wireOp",EDGE,"E75.6.2")])]})]});
            var Q5;
            Q5=makeQuery(id+"F12.boolean.opBoolean","INTERSECT",EDGE,{"derivedFrom":[makeQuery(id+"F9.opRevolve","SWEPT_FACE",FACE,{"disambiguationData":[OSD([sQuery(id+"F8.wireOp",EDGE,"E55.right")])]}),makeQuery(id+"F12.opExtrude","SWEPT_FACE",FACE,{"disambiguationData":[OSD([sQuery(id+"F11.wireOp",EDGE,"E75.7.1")])]})]});
            var Q6;
            Q6=makeQuery(id+"F12.boolean.opBoolean","INTERSECT",EDGE,{"derivedFrom":[makeQuery(id+"F9.opRevolve","SWEPT_FACE",FACE,{"disambiguationData":[OSD([sQuery(id+"F8.wireOp",EDGE,"E55.right")])]}),makeQuery(id+"F12.opExtrude","SWEPT_FACE",FACE,{"disambiguationData":[OSD([sQuery(id+"F11.wireOp",EDGE,"E75.7.2")])]})]});
            var Q7;
            Q7=makeQuery(id+"F12.boolean.opBoolean","INTERSECT",EDGE,{"derivedFrom":[makeQuery(id+"F9.opRevolve","SWEPT_FACE",FACE,{"disambiguationData":[OSD([sQuery(id+"F8.wireOp",EDGE,"E55.right")])]}),makeQuery(id+"F12.opExtrude","SWEPT_FACE",FACE,{"disambiguationData":[OSD([sQuery(id+"F11.wireOp",EDGE,"E74")])]})]});
            var Q8;
            Q8=makeQuery(id+"F12.boolean.opBoolean","INTERSECT",EDGE,{"derivedFrom":[makeQuery(id+"F9.opRevolve","SWEPT_FACE",FACE,{"disambiguationData":[OSD([sQuery(id+"F8.wireOp",EDGE,"E55.left")])]}),makeQuery(id+"F12.opExtrude","SWEPT_FACE",FACE,{"disambiguationData":[OSD([sQuery(id+"F11.wireOp",EDGE,"E74")])]})]});
            var Q9;
            Q9=makeQuery(id+"F12.boolean.opBoolean","INTERSECT",EDGE,{"derivedFrom":[makeQuery(id+"F9.opRevolve","SWEPT_FACE",FACE,{"disambiguationData":[OSD([sQuery(id+"F8.wireOp",EDGE,"E55.left")])]}),makeQuery(id+"F12.opExtrude","SWEPT_FACE",FACE,{"disambiguationData":[OSD([sQuery(id+"F11.wireOp",EDGE,"E75.7.2")])]})]});
            var Q10;
            Q10=makeQuery(id+"F12.boolean.opBoolean","INTERSECT",EDGE,{"derivedFrom":[makeQuery(id+"F9.opRevolve","SWEPT_FACE",FACE,{"disambiguationData":[OSD([sQuery(id+"F8.wireOp",EDGE,"E55.left")])]}),makeQuery(id+"F12.opExtrude","SWEPT_FACE",FACE,{"disambiguationData":[OSD([sQuery(id+"F11.wireOp",EDGE,"E73")])]})]});
            var Q11;
            Q11=makeQuery(id+"F12.boolean.opBoolean","INTERSECT",EDGE,{"derivedFrom":[makeQuery(id+"F9.opRevolve","SWEPT_FACE",FACE,{"disambiguationData":[OSD([sQuery(id+"F8.wireOp",EDGE,"E55.right")])]}),makeQuery(id+"F12.opExtrude","SWEPT_FACE",FACE,{"disambiguationData":[OSD([sQuery(id+"F11.wireOp",EDGE,"E73")])]})]});
            var Q12;
            Q12=makeQuery(id+"F12.boolean.opBoolean","INTERSECT",EDGE,{"derivedFrom":[makeQuery(id+"F9.opRevolve","SWEPT_FACE",FACE,{"disambiguationData":[OSD([sQuery(id+"F8.wireOp",EDGE,"E55.right")])]}),makeQuery(id+"F12.opExtrude","SWEPT_FACE",FACE,{"disambiguationData":[OSD([sQuery(id+"F11.wireOp",EDGE,"E75.1.1")])]})]});
            var Q13;
            Q13=makeQuery(id+"F12.boolean.opBoolean","INTERSECT",EDGE,{"derivedFrom":[makeQuery(id+"F9.opRevolve","SWEPT_FACE",FACE,{"disambiguationData":[OSD([sQuery(id+"F8.wireOp",EDGE,"E55.left")])]}),makeQuery(id+"F12.opExtrude","SWEPT_FACE",FACE,{"disambiguationData":[OSD([sQuery(id+"F11.wireOp",EDGE,"E75.1.1")])]})]});
            var Q14;
            Q14=makeQuery(id+"F12.boolean.opBoolean","INTERSECT",EDGE,{"derivedFrom":[makeQuery(id+"F9.opRevolve","SWEPT_FACE",FACE,{"disambiguationData":[OSD([sQuery(id+"F8.wireOp",EDGE,"E55.left")])]}),makeQuery(id+"F12.opExtrude","SWEPT_FACE",FACE,{"disambiguationData":[OSD([sQuery(id+"F11.wireOp",EDGE,"E75.2.1")])]})]});
            var Q15;
            Q15=makeQuery(id+"F12.boolean.opBoolean","INTERSECT",EDGE,{"derivedFrom":[makeQuery(id+"F9.opRevolve","SWEPT_FACE",FACE,{"disambiguationData":[OSD([sQuery(id+"F8.wireOp",EDGE,"E55.right")])]}),makeQuery(id+"F12.opExtrude","SWEPT_FACE",FACE,{"disambiguationData":[OSD([sQuery(id+"F11.wireOp",EDGE,"E75.2.1")])]})]});
            var Q16;
            Q16=makeQuery(id+"F12.boolean.opBoolean","INTERSECT",EDGE,{"derivedFrom":[makeQuery(id+"F9.opRevolve","SWEPT_FACE",FACE,{"disambiguationData":[OSD([sQuery(id+"F8.wireOp",EDGE,"E55.left")])]}),makeQuery(id+"F12.opExtrude","SWEPT_FACE",FACE,{"disambiguationData":[OSD([sQuery(id+"F11.wireOp",EDGE,"E75.2.2")])]})]});
            var Q17;
            Q17=makeQuery(id+"F12.boolean.opBoolean","INTERSECT",EDGE,{"derivedFrom":[makeQuery(id+"F9.opRevolve","SWEPT_FACE",FACE,{"disambiguationData":[OSD([sQuery(id+"F8.wireOp",EDGE,"E55.left")])]}),makeQuery(id+"F12.opExtrude","SWEPT_FACE",FACE,{"disambiguationData":[OSD([sQuery(id+"F11.wireOp",EDGE,"E75.3.1")])]})]});
            var Q18;
            Q18=makeQuery(id+"F12.boolean.opBoolean","INTERSECT",EDGE,{"derivedFrom":[makeQuery(id+"F9.opRevolve","SWEPT_FACE",FACE,{"disambiguationData":[OSD([sQuery(id+"F8.wireOp",EDGE,"E55.left")])]}),makeQuery(id+"F12.opExtrude","SWEPT_FACE",FACE,{"disambiguationData":[OSD([sQuery(id+"F11.wireOp",EDGE,"E75.3.2")])]})]});
            var Q19;
            Q19=makeQuery(id+"F12.boolean.opBoolean","INTERSECT",EDGE,{"derivedFrom":[makeQuery(id+"F9.opRevolve","SWEPT_FACE",FACE,{"disambiguationData":[OSD([sQuery(id+"F8.wireOp",EDGE,"E55.left")])]}),makeQuery(id+"F12.opExtrude","SWEPT_FACE",FACE,{"disambiguationData":[OSD([sQuery(id+"F11.wireOp",EDGE,"E75.4.1")])]})]});
            var Q20;
            Q20=makeQuery(id+"F12.boolean.opBoolean","INTERSECT",EDGE,{"derivedFrom":[makeQuery(id+"F9.opRevolve","SWEPT_FACE",FACE,{"disambiguationData":[OSD([sQuery(id+"F8.wireOp",EDGE,"E55.right")])]}),makeQuery(id+"F12.opExtrude","SWEPT_FACE",FACE,{"disambiguationData":[OSD([sQuery(id+"F11.wireOp",EDGE,"E75.4.2")])]})]});
            var Q21;
            Q21=makeQuery(id+"F12.boolean.opBoolean","INTERSECT",EDGE,{"derivedFrom":[makeQuery(id+"F9.opRevolve","SWEPT_FACE",FACE,{"disambiguationData":[OSD([sQuery(id+"F8.wireOp",EDGE,"E55.left")])]}),makeQuery(id+"F12.opExtrude","SWEPT_FACE",FACE,{"disambiguationData":[OSD([sQuery(id+"F11.wireOp",EDGE,"E75.4.2")])]})]});
            var Q22;
            Q22=makeQuery(id+"F12.boolean.opBoolean","INTERSECT",EDGE,{"derivedFrom":[makeQuery(id+"F9.opRevolve","SWEPT_FACE",FACE,{"disambiguationData":[OSD([sQuery(id+"F8.wireOp",EDGE,"E55.right")])]}),makeQuery(id+"F12.opExtrude","SWEPT_FACE",FACE,{"disambiguationData":[OSD([sQuery(id+"F11.wireOp",EDGE,"E75.5.2")])]})]});
            var Q23;
            Q23=makeQuery(id+"F12.boolean.opBoolean","INTERSECT",EDGE,{"derivedFrom":[makeQuery(id+"F9.opRevolve","SWEPT_FACE",FACE,{"disambiguationData":[OSD([sQuery(id+"F8.wireOp",EDGE,"E55.left")])]}),makeQuery(id+"F12.opExtrude","SWEPT_FACE",FACE,{"disambiguationData":[OSD([sQuery(id+"F11.wireOp",EDGE,"E75.5.2")])]})]});
            var Q24;
            Q24=makeQuery(id+"F12.boolean.opBoolean","INTERSECT",EDGE,{"derivedFrom":[makeQuery(id+"F9.opRevolve","SWEPT_FACE",FACE,{"disambiguationData":[OSD([sQuery(id+"F8.wireOp",EDGE,"E55.left")])]}),makeQuery(id+"F12.opExtrude","SWEPT_FACE",FACE,{"disambiguationData":[OSD([sQuery(id+"F11.wireOp",EDGE,"E75.5.1")])]})]});
            var Q25;
            Q25=makeQuery(id+"F12.boolean.opBoolean","INTERSECT",EDGE,{"derivedFrom":[makeQuery(id+"F9.opRevolve","SWEPT_FACE",FACE,{"disambiguationData":[OSD([sQuery(id+"F8.wireOp",EDGE,"E55.right")])]}),makeQuery(id+"F12.opExtrude","SWEPT_FACE",FACE,{"disambiguationData":[OSD([sQuery(id+"F11.wireOp",EDGE,"E75.5.1")])]})]});
            var Q26;
            Q26=makeQuery(id+"F12.boolean.opBoolean","INTERSECT",EDGE,{"derivedFrom":[makeQuery(id+"F9.opRevolve","SWEPT_FACE",FACE,{"disambiguationData":[OSD([sQuery(id+"F8.wireOp",EDGE,"E55.right")])]}),makeQuery(id+"F12.opExtrude","SWEPT_FACE",FACE,{"disambiguationData":[OSD([sQuery(id+"F11.wireOp",EDGE,"E75.4.1")])]})]});
            var Q27;
            Q27=makeQuery(id+"F12.boolean.opBoolean","INTERSECT",EDGE,{"derivedFrom":[makeQuery(id+"F9.opRevolve","SWEPT_FACE",FACE,{"disambiguationData":[OSD([sQuery(id+"F8.wireOp",EDGE,"E55.right")])]}),makeQuery(id+"F12.opExtrude","SWEPT_FACE",FACE,{"disambiguationData":[OSD([sQuery(id+"F11.wireOp",EDGE,"E75.3.2")])]})]});
            var Q28;
            Q28=makeQuery(id+"F12.boolean.opBoolean","INTERSECT",EDGE,{"derivedFrom":[makeQuery(id+"F9.opRevolve","SWEPT_FACE",FACE,{"disambiguationData":[OSD([sQuery(id+"F8.wireOp",EDGE,"E55.right")])]}),makeQuery(id+"F12.opExtrude","SWEPT_FACE",FACE,{"disambiguationData":[OSD([sQuery(id+"F11.wireOp",EDGE,"E75.3.1")])]})]});
            var Q29;
            Q29=makeQuery(id+"F12.boolean.opBoolean","INTERSECT",EDGE,{"derivedFrom":[makeQuery(id+"F9.opRevolve","SWEPT_FACE",FACE,{"disambiguationData":[OSD([sQuery(id+"F8.wireOp",EDGE,"E55.right")])]}),makeQuery(id+"F12.opExtrude","SWEPT_FACE",FACE,{"disambiguationData":[OSD([sQuery(id+"F11.wireOp",EDGE,"E75.2.2")])]})]});
            var Q30;
            Q30=makeQuery(id+"F12.boolean.opBoolean","INTERSECT",EDGE,{"derivedFrom":[makeQuery(id+"F9.opRevolve","SWEPT_FACE",FACE,{"disambiguationData":[OSD([sQuery(id+"F8.wireOp",EDGE,"E55.right")])]}),makeQuery(id+"F12.opExtrude","SWEPT_FACE",FACE,{"disambiguationData":[OSD([sQuery(id+"F11.wireOp",EDGE,"E75.1.2")])]})]});
            var Q31;
            Q31=makeQuery(id+"F12.boolean.opBoolean","INTERSECT",EDGE,{"derivedFrom":[makeQuery(id+"F9.opRevolve","SWEPT_FACE",FACE,{"disambiguationData":[OSD([sQuery(id+"F8.wireOp",EDGE,"E55.left")])]}),makeQuery(id+"F12.opExtrude","SWEPT_FACE",FACE,{"disambiguationData":[OSD([sQuery(id+"F11.wireOp",EDGE,"E75.1.2")])]})]});
            fillet(context, id + "F14", {"entities" : qUnion([Q0, Q1, Q2, Q3, Q4, Q5, Q6, Q7, Q8, Q9, Q10, Q11, Q12, Q13, Q14, Q15, Q16, Q17, Q18, Q19, Q20, Q21, Q22, Q23, Q24, Q25, Q26, Q27, Q28, Q29, Q30, Q31]), "radius" : 0.25 * mm, "tangentPropagation" : true, "allowEdgeOverflow" : false});
        }
        {
            var Q0;
            Q0=qCreatedBy(makeId("Right.planeOp"),FACE);
            var sketch = newSketch(context, id + "F15", { "sketchPlane" : qUnion([Q0])});
            skLineSegment(sketch, "E76", {"start": v(-4.85, 0) * mm, "end": v(-6.31, 0) * mm});
            skLineSegment(sketch, "E77", {"start": v(0, 3.44) * mm, "end": v(0, 0) * mm});
            skLineSegment(sketch, "E78", {"start": v(0, 0) * mm, "end": v(15.35, 1.34) * mm});
            skLineSegment(sketch, "E79.bottom", {"start": v(-29.8, -3.61) * mm, "end": v(29.97, 1.62) * mm});
            skLineSegment(sketch, "E79.top", {"start": v(-29.97, -1.62) * mm, "end": v(29.8, 3.61) * mm});
            skLineSegment(sketch, "E79.left", {"start": v(-29.8, -3.61) * mm, "end": v(-29.97, -1.62) * mm});
            skLineSegment(sketch, "E79.right", {"start": v(29.97, 1.62) * mm, "end": v(29.8, 3.61) * mm});
            skPoint(sketch, "E79.middle", {"position": v(0, 0) * mm});
            skLineSegment(sketch, "E80.bottom", {"start": v(-2.85, -4.58) * mm, "end": v(2.85, -4.58) * mm});
            skLineSegment(sketch, "E80.top", {"start": v(-2.85, 4.58) * mm, "end": v(2.85, 4.58) * mm});
            skLineSegment(sketch, "E80.left", {"start": v(-2.85, -4.58) * mm, "end": v(-2.85, -1.25) * mm});
            skLineSegment(sketch, "E80.right", {"start": v(2.85, -4.58) * mm, "end": v(2.85, 4.58) * mm});
            skLineSegment(sketch, "E81.bottom", {"start": v(-4.85, -4.58) * mm, "end": v(4.85, -4.58) * mm});
            skLineSegment(sketch, "E81.top", {"start": v(-4.85, 4.58) * mm, "end": v(4.85, 4.58) * mm});
            skLineSegment(sketch, "E81.left", {"start": v(-4.85, -4.58) * mm, "end": v(-4.85, -1.43) * mm});
            skLineSegment(sketch, "E81.right", {"start": v(4.85, -4.58) * mm, "end": v(4.85, 4.58) * mm});
            skLineSegment(sketch, "E82", {"start": v(0, 0) * mm, "end": v(-0.22, 2.56) * mm});
            skLineSegment(sketch, "E83.trimOffspring", {"start": v(-2.85, 0.75) * mm, "end": v(-2.85, 4.58) * mm});
            skLineSegment(sketch, "E84.trimOffspring", {"start": v(-4.85, 0.58) * mm, "end": v(-4.85, 4.58) * mm});
            skLineSegment(sketch, "E85", {"start": v(0, 0) * mm, "end": v(0.09, -1) * mm});
            skLineSegment(sketch, "E86.trimOffspring", {"start": v(0, -1) * mm, "end": v(0, -3.76) * mm});
            skSolve(sketch);
        }
        {
            var Q0;
            Q0=qCreatedBy(makeId("Right.planeOp"),FACE);
            var sketch = newSketch(context, id + "F16", { "sketchPlane" : qUnion([Q0])});
            skLineSegment(sketch, "E87.bottom", {"start": v(-25, 8.46) * mm, "end": v(-34.51, 8.46) * mm});
            skLineSegment(sketch, "E87.top", {"start": v(-25, -11.25) * mm, "end": v(-34.51, -11.25) * mm});
            skLineSegment(sketch, "E87.left", {"start": v(-25, 8.46) * mm, "end": v(-25, -11.25) * mm});
            skLineSegment(sketch, "E87.right", {"start": v(-34.51, 8.46) * mm, "end": v(-34.51, -11.25) * mm});
            skSolve(sketch);
        }
        {
            var Q0;
            {var subQ3=sQuery(id+"F15.wireOp",EDGE,"E79.left");Q0=makeQuery(id+"F15.imprint","IMPRINT",FACE,{"disambiguationData":[TD([[makeQuery(id+"F15.imprint","IMPRINT",EDGE,{"derivedFrom":subQ3}),-1.0]])]});}
            var Q1;
            Q1=sQuery(id+"F15.wireOp",EDGE,"E82");
            revolve(context, id + "F17", {"surfaceOperationType" : NewSurfaceOperationType.NEW, "entities" : qUnion([Q0]), "axis" : qUnion([Q1]), "revolveType" : RevolveType.FULL});
        }
        {
            var Q0;
            Q0=makeQuery(id+"F16.imprint","IMPRINT",FACE,{"disambiguationData":[TD([[makeQuery(id+"F16.imprint","IMPRINT",EDGE,{"derivedFrom":sQuery(id+"F16.wireOp",EDGE,"E87.bottom")}),1.0]])]});
            var Q1;
            Q1=sQuery(id+"F15.wireOp",EDGE,"E77");
            revolve(context, id + "F18", {"operationType" : NewBodyOperationType.REMOVE, "surfaceOperationType" : NewSurfaceOperationType.NEW, "entities" : qUnion([Q0]), "axis" : qUnion([Q1]), "revolveType" : RevolveType.FULL, "oppositeDirection" : true});
        }
        {
            var Q0;
            Q0=qCreatedBy(makeId("Right.planeOp"),FACE);
            var sketch = newSketch(context, id + "F19", { "sketchPlane" : qUnion([Q0])});
            skLineSegment(sketch, "E88.bottom", {"start": v(0, -3) * mm, "end": v(2.85, -3) * mm});
            skLineSegment(sketch, "E88.top", {"start": v(0, 3) * mm, "end": v(2.85, 3) * mm});
            skLineSegment(sketch, "E88.left", {"start": v(0, -3) * mm, "end": v(0, 3) * mm});
            skLineSegment(sketch, "E88.right", {"start": v(2.85, -3) * mm, "end": v(2.85, 3) * mm});
            skSolve(sketch);
        }
        {
            var Q0;
            Q0=makeQuery(id+"F19.imprint","IMPRINT",FACE,{"disambiguationData":[TD([[makeQuery(id+"F19.imprint","IMPRINT",EDGE,{"derivedFrom":sQuery(id+"F19.wireOp",EDGE,"E88.bottom")}),1.0]])]});
            var Q1;
            Q1=sQuery(id+"F15.wireOp",EDGE,"E77");
            revolve(context, id + "F20", {"operationType" : NewBodyOperationType.REMOVE, "surfaceOperationType" : NewSurfaceOperationType.NEW, "entities" : qUnion([Q0]), "axis" : qUnion([Q1]), "revolveType" : RevolveType.FULL, "oppositeDirection" : true});
        }
        {
            var Q0;
            {var subQ0=sQuery(id+"F15.wireOp",EDGE,"E81.right");var subQ1=sQuery(id+"F15.wireOp",EDGE,"E79.top");var subQ2=makeQuery(id+"F15.imprint","INTERSECT",VERTEX,{"derivedFrom":[subQ1,subQ0]});Q0=makeQuery(id+"F15.imprint","IMPRINT",FACE,{"disambiguationData":[TD([[makeQuery(id+"F15.imprint","IMPRINT",EDGE,{"disambiguationData":[TD([[subQ2,1.0]])],"derivedFrom":subQ1}),1.0]])]});}
            var Q1;
            {var subQ0=sQuery(id+"F15.wireOp",EDGE,"E81.right");var subQ1=sQuery(id+"F15.wireOp",EDGE,"E78");var subQ2=makeQuery(id+"F15.imprint","INTERSECT",VERTEX,{"derivedFrom":[subQ1,subQ0]});Q1=makeQuery(id+"F15.imprint","IMPRINT",FACE,{"disambiguationData":[TD([[makeQuery(id+"F15.imprint","IMPRINT",EDGE,{"disambiguationData":[TD([[subQ2,1.0]])],"derivedFrom":subQ1}),1.0]])]});}
            var Q2;
            {var subQ0=sQuery(id+"F15.wireOp",EDGE,"E81.right");var subQ1=sQuery(id+"F15.wireOp",EDGE,"E78");var subQ2=makeQuery(id+"F15.imprint","INTERSECT",VERTEX,{"derivedFrom":[subQ1,subQ0]});Q2=makeQuery(id+"F15.imprint","IMPRINT",FACE,{"disambiguationData":[TD([[makeQuery(id+"F15.imprint","IMPRINT",EDGE,{"disambiguationData":[TD([[subQ2,1.0]])],"derivedFrom":subQ1}),-1.0]])]});}
            var Q3;
            {var subQ0=sQuery(id+"F15.wireOp",EDGE,"E81.right");var subQ1=sQuery(id+"F15.wireOp",EDGE,"E79.bottom");var subQ2=makeQuery(id+"F15.imprint","INTERSECT",VERTEX,{"derivedFrom":[subQ1,subQ0]});Q3=makeQuery(id+"F15.imprint","IMPRINT",FACE,{"disambiguationData":[TD([[makeQuery(id+"F15.imprint","IMPRINT",EDGE,{"disambiguationData":[TD([[subQ2,1.0]])],"derivedFrom":subQ1}),-1.0]])]});}
            var Q4;
            Q4=sQuery(id+"F15.wireOp",EDGE,"E77");
            revolve(context, id + "F21", {"operationType" : NewBodyOperationType.ADD, "surfaceOperationType" : NewSurfaceOperationType.NEW, "entities" : qUnion([Q0, Q1, Q2, Q3]), "axis" : qUnion([Q4]), "revolveType" : RevolveType.FULL});
        }
        {
            var Q0;
            Q0=makeQuery(id+"F18.boolean.opBoolean","INTERSECT",EDGE,{"derivedFrom":[makeQuery(id+"F17.opRevolve","SWEPT_FACE",FACE,{"disambiguationData":[OSD([sQuery(id+"F15.wireOp",EDGE,"E79.top")])]}),makeQuery(id+"F18.opRevolve","SWEPT_FACE",FACE,{"disambiguationData":[OSD([sQuery(id+"F16.wireOp",EDGE,"E87.left")])]})]});
            var Q1;
            Q1=makeQuery(id+"F18.boolean.opBoolean","INTERSECT",EDGE,{"derivedFrom":[makeQuery(id+"F17.opRevolve","SWEPT_FACE",FACE,{"disambiguationData":[OSD([sQuery(id+"F15.wireOp",EDGE,"E79.bottom")])]}),makeQuery(id+"F18.opRevolve","SWEPT_FACE",FACE,{"disambiguationData":[OSD([sQuery(id+"F16.wireOp",EDGE,"E87.left")])]})]});
            var Q2;
            Q2=makeQuery(id+"F21.opRevolve","SWEPT_EDGE",EDGE,{"disambiguationData":[OSD([sQuery(id+"F15.wireOp",EDGE,"E81.top"),sQuery(id+"F15.wireOp",EDGE,"E81.right")])]});
            var Q3;
            Q3=makeQuery(id+"F21.opRevolve","SWEPT_EDGE",EDGE,{"disambiguationData":[OSD([sQuery(id+"F15.wireOp",EDGE,"E81.bottom"),sQuery(id+"F15.wireOp",EDGE,"E81.right")])]});
            var Q4;
            Q4=makeQuery(id+"F21.boolean.opBoolean","INTERSECT",EDGE,{"derivedFrom":[makeQuery(id+"F17.opRevolve","SWEPT_FACE",FACE,{"disambiguationData":[OSD([sQuery(id+"F15.wireOp",EDGE,"E79.bottom")])]}),makeQuery(id+"F21.opRevolve","SWEPT_FACE",FACE,{"disambiguationData":[OSD([sQuery(id+"F15.wireOp",EDGE,"E81.right")])]})]});
            var Q5;
            Q5=makeQuery(id+"F21.boolean.opBoolean","INTERSECT",EDGE,{"derivedFrom":[makeQuery(id+"F17.opRevolve","SWEPT_FACE",FACE,{"disambiguationData":[OSD([sQuery(id+"F15.wireOp",EDGE,"E79.top")])]}),makeQuery(id+"F21.opRevolve","SWEPT_FACE",FACE,{"disambiguationData":[OSD([sQuery(id+"F15.wireOp",EDGE,"E81.right")])]})]});
            fillet(context, id + "F22", {"entities" : qUnion([Q0, Q1, Q2, Q3, Q4, Q5]), "radius" : .25 * mm, "tangentPropagation" : true, "allowEdgeOverflow" : false});
        }
        {
            var Q0;
            Q0=qCreatedBy(makeId("Right.planeOp"),FACE);
            var sketch = newSketch(context, id + "F23", { "sketchPlane" : qUnion([Q0])});
            skLineSegment(sketch, "E89.top", {"start": v(-4.41, 74.25) * mm, "end": v(-2.91, 74.25) * mm});
            skLineSegment(sketch, "E89.right", {"start": v(-2.91, 61.55) * mm, "end": v(-2.91, 74.25) * mm});
            skPoint(sketch, "E89.middle", {"position": v(-4.41, 65.51) * mm});
            skLineSegment(sketch, "E90.bottom", {"start": v(-0.91, 76.25) * mm, "end": v(-4.41, 76.25) * mm});
            skLineSegment(sketch, "E90.left", {"start": v(-0.91, 76.25) * mm, "end": v(-0.91, 64.06) * mm});
            skLineSegment(sketch, "E91", {"start": v(-4.41, 74.25) * mm, "end": v(-4.41, 76.25) * mm});
            skPoint(sketch, "E92.orphan", {"position": v(-5.91, 74.25) * mm});
            skArc(sketch, "E93.trimOffspring", {"start": v(-0.91, 64.06) * mm, "mid": v(5.94, 75.74) * mm, "end": v(-4.41, 84.46) * mm});
            skArc(sketch, "E94.trimOffspring", {"start": v(-2.91, 61.55) * mm, "mid": v(8.12, 74.71) * mm, "end": v(-4.41, 86.46) * mm});
            skPoint(sketch, "E89.bottom.end.orphan", {"position": v(-2.91, 56.77) * mm});
            skPoint(sketch, "E89.bottom.start.orphan", {"position": v(-5.91, 56.77) * mm});
            skLineSegment(sketch, "E95.trimOffspring", {"start": v(-4.41, 84.46) * mm, "end": v(-4.41, 92.3) * mm});
            skArc(sketch, "E96", {"start": v(-43.63, 35.22) * mm, "mid": v(-39.64, 40.29) * mm, "end": v(-44.38, 44.66) * mm});
            skLineSegment(sketch, "E97.top", {"start": v(-44.38, 40.22) * mm, "end": v(-43.63, 40.22) * mm});
            skLineSegment(sketch, "E97.right", {"start": v(-43.63, 35.22) * mm, "end": v(-43.63, 40.22) * mm});
            skPoint(sketch, "E97.middle", {"position": v(-44.38, 37.72) * mm});
            skLineSegment(sketch, "E98.top", {"start": v(-44.38, 41.22) * mm, "end": v(-43.13, 41.22) * mm});
            skLineSegment(sketch, "E98.right", {"start": v(-42.63, 37.79) * mm, "end": v(-42.63, 40.72) * mm});
            skLineSegment(sketch, "E99", {"start": v(-44.38, 40.22) * mm, "end": v(-44.38, 41.22) * mm});
            skPoint(sketch, "E99.endSnap0", {"position": v(-44.38, 41.22) * mm});
            skPoint(sketch, "E100.orphan", {"position": v(-46.13, 41.22) * mm});
            skLineSegment(sketch, "E101.trimOffspring", {"start": v(-44.38, 42.66) * mm, "end": v(-44.38, 45.22) * mm});
            skPoint(sketch, "E102.orphan", {"position": v(-45.13, 40.22) * mm});
            skArc(sketch, "E103.trimOffspring", {"start": v(-42.63, 37.79) * mm, "mid": v(-41.8, 40.84) * mm, "end": v(-44.38, 42.66) * mm});
            skPoint(sketch, "E104.orphan", {"position": v(-45.13, 35.22) * mm});
            skPoint(sketch, "E98.left.start.orphan", {"position": v(-46.13, 34.22) * mm});
            skPoint(sketch, "E105.orphan", {"position": v(-42.63, 34.22) * mm});
            skPoint(sketch, "E106.visualSharp", {"position": v(-42.63, 41.22) * mm});
            skArc(sketch, "E106.filletArc", {"start": v(-42.63, 40.72) * mm, "mid": v(-42.78, 41.07) * mm, "end": v(-43.13, 41.22) * mm});
            skSolve(sketch);
        }
        {
            var Q0;
            Q0=makeQuery(id+"F23.imprint","IMPRINT",FACE,{"disambiguationData":[TD([[makeQuery(id+"F23.imprint","IMPRINT",EDGE,{"derivedFrom":sQuery(id+"F23.wireOp",EDGE,"E89.top")}),1.0]])]});
            var Q1;
            Q1=sQuery(id+"F23.wireOp",EDGE,"E95.trimOffspring");
            revolve(context, id + "F24", {"surfaceOperationType" : NewSurfaceOperationType.NEW, "entities" : qUnion([Q0]), "axis" : qUnion([Q1]), "revolveType" : RevolveType.FULL});
        }
        {
            var Q0;
            Q0=makeQuery(id+"F9.opRevolve","SWEPT_FACE",FACE,{"disambiguationData":[OSD([sQuery(id+"F8.wireOp",EDGE,"E58.trimOffspring")])]});
            var sketch = newSketch(context, id + "F25", { "sketchPlane" : qUnion([Q0])});
            skCircle(sketch, "E107", {"center": v(0, 94.42) * mm, "radius": 3.1 * mm});
            skArc(sketch, "E108", {"start": v(-2.21, 96.29) * mm, "mid": v(-2.62, 95.65) * mm, "end": v(-2.85, 94.93) * mm});
            skLineSegment(sketch, "E109", {"start": v(-2.85, 94.93) * mm, "end": v(-3.05, 94.97) * mm});
            skLineSegment(sketch, "E110", {"start": v(-2.21, 96.29) * mm, "end": v(-2.37, 96.42) * mm});
            skLineSegment(sketch, "E111.1.0", {"start": v(-1.87, 92.2) * mm, "end": v(-2, 92.05) * mm});
            skArc(sketch, "E111.1.1", {"start": v(-2.73, 93.44) * mm, "mid": v(-2.38, 92.76) * mm, "end": v(-1.87, 92.2) * mm});
            skLineSegment(sketch, "E111.1.2", {"start": v(-2.73, 93.44) * mm, "end": v(-2.92, 93.37) * mm});
            skLineSegment(sketch, "E111.2.0", {"start": v(0.98, 91.69) * mm, "end": v(1.05, 91.5) * mm});
            skArc(sketch, "E111.2.1", {"start": v(-0.51, 91.56) * mm, "mid": v(0.24, 91.53) * mm, "end": v(0.98, 91.69) * mm});
            skLineSegment(sketch, "E111.2.2", {"start": v(-0.51, 91.56) * mm, "end": v(-0.55, 91.37) * mm});
            skLineSegment(sketch, "E111.3.0", {"start": v(2.85, 93.9) * mm, "end": v(3.05, 93.87) * mm});
            skArc(sketch, "E111.3.1", {"start": v(2.21, 92.54) * mm, "mid": v(2.62, 93.18) * mm, "end": v(2.85, 93.9) * mm});
            skLineSegment(sketch, "E111.3.2", {"start": v(2.21, 92.54) * mm, "end": v(2.37, 92.42) * mm});
            skLineSegment(sketch, "E111.4.0", {"start": v(1.87, 96.63) * mm, "end": v(2, 96.78) * mm});
            skArc(sketch, "E111.4.1", {"start": v(2.73, 95.4) * mm, "mid": v(2.38, 96.07) * mm, "end": v(1.87, 96.63) * mm});
            skLineSegment(sketch, "E111.4.2", {"start": v(2.73, 95.4) * mm, "end": v(2.92, 95.47) * mm});
            skLineSegment(sketch, "E111.5.0", {"start": v(-0.98, 97.15) * mm, "end": v(-1.05, 97.33) * mm});
            skArc(sketch, "E111.5.1", {"start": v(0.51, 97.27) * mm, "mid": v(-0.24, 97.3) * mm, "end": v(-0.98, 97.15) * mm});
            skLineSegment(sketch, "E111.5.2", {"start": v(0.51, 97.27) * mm, "end": v(0.55, 97.47) * mm});
            skSolve(sketch);
        }
        {
            var Q0;
            {var subQ0=sQuery(id+"F25.wireOp",EDGE,"E108");Q0=makeQuery(id+"F25.imprint","IMPRINT",FACE,{"disambiguationData":[TD([[makeQuery(id+"F25.imprint","IMPRINT",EDGE,{"derivedFrom":subQ0}),-1.0]])]});}
            var Q1;
            {var subQ0=sQuery(id+"F25.wireOp",EDGE,"E109");var subQ1=sQuery(id+"F25.wireOp",EDGE,"E107");var subQ2=makeQuery(id+"F25.imprint","INTERSECT",VERTEX,{"derivedFrom":[subQ1,subQ0]});Q1=makeQuery(id+"F25.imprint","IMPRINT",FACE,{"disambiguationData":[TD([[makeQuery(id+"F25.imprint","IMPRINT",EDGE,{"disambiguationData":[TD([[subQ2,1.0]])],"derivedFrom":subQ1}),1.0]])]});}
            var Q2;
            {var subQ0=sQuery(id+"F25.wireOp",EDGE,"E111.5.0");var subQ1=sQuery(id+"F25.wireOp",EDGE,"E107");var subQ2=makeQuery(id+"F25.imprint","INTERSECT",VERTEX,{"derivedFrom":[subQ1,subQ0]});Q2=makeQuery(id+"F25.imprint","IMPRINT",FACE,{"disambiguationData":[TD([[makeQuery(id+"F25.imprint","IMPRINT",EDGE,{"disambiguationData":[TD([[subQ2,1.0]])],"derivedFrom":subQ1}),1.0]])]});}
            var Q3;
            {var subQ0=sQuery(id+"F25.wireOp",EDGE,"E111.5.1");Q3=makeQuery(id+"F25.imprint","IMPRINT",FACE,{"disambiguationData":[TD([[makeQuery(id+"F25.imprint","IMPRINT",EDGE,{"derivedFrom":subQ0}),-1.0]])]});}
            var Q4;
            {var subQ0=sQuery(id+"F25.wireOp",EDGE,"E111.4.0");var subQ1=sQuery(id+"F25.wireOp",EDGE,"E107");var subQ2=makeQuery(id+"F25.imprint","INTERSECT",VERTEX,{"derivedFrom":[subQ1,subQ0]});Q4=makeQuery(id+"F25.imprint","IMPRINT",FACE,{"disambiguationData":[TD([[makeQuery(id+"F25.imprint","IMPRINT",EDGE,{"disambiguationData":[TD([[subQ2,1.0]])],"derivedFrom":subQ1}),1.0]])]});}
            var Q5;
            {var subQ0=sQuery(id+"F25.wireOp",EDGE,"E111.4.1");Q5=makeQuery(id+"F25.imprint","IMPRINT",FACE,{"disambiguationData":[TD([[makeQuery(id+"F25.imprint","IMPRINT",EDGE,{"derivedFrom":subQ0}),-1.0]])]});}
            var Q6;
            {var subQ0=sQuery(id+"F25.wireOp",EDGE,"E111.3.0");var subQ1=sQuery(id+"F25.wireOp",EDGE,"E107");var subQ2=makeQuery(id+"F25.imprint","INTERSECT",VERTEX,{"derivedFrom":[subQ1,subQ0]});Q6=makeQuery(id+"F25.imprint","IMPRINT",FACE,{"disambiguationData":[TD([[makeQuery(id+"F25.imprint","IMPRINT",EDGE,{"disambiguationData":[TD([[subQ2,1.0]])],"derivedFrom":subQ1}),1.0]])]});}
            var Q7;
            {var subQ0=sQuery(id+"F25.wireOp",EDGE,"E111.3.1");Q7=makeQuery(id+"F25.imprint","IMPRINT",FACE,{"disambiguationData":[TD([[makeQuery(id+"F25.imprint","IMPRINT",EDGE,{"derivedFrom":subQ0}),-1.0]])]});}
            var Q8;
            {var subQ0=sQuery(id+"F25.wireOp",EDGE,"E111.2.1");Q8=makeQuery(id+"F25.imprint","IMPRINT",FACE,{"disambiguationData":[TD([[makeQuery(id+"F25.imprint","IMPRINT",EDGE,{"derivedFrom":subQ0}),-1.0]])]});}
            var Q9;
            {var subQ0=sQuery(id+"F25.wireOp",EDGE,"E111.2.0");var subQ1=sQuery(id+"F25.wireOp",EDGE,"E107");var subQ2=makeQuery(id+"F25.imprint","INTERSECT",VERTEX,{"derivedFrom":[subQ1,subQ0]});Q9=makeQuery(id+"F25.imprint","IMPRINT",FACE,{"disambiguationData":[TD([[makeQuery(id+"F25.imprint","IMPRINT",EDGE,{"disambiguationData":[TD([[subQ2,1.0]])],"derivedFrom":subQ1}),1.0]])]});}
            var Q10;
            {var subQ0=sQuery(id+"F25.wireOp",EDGE,"E111.1.0");var subQ1=sQuery(id+"F25.wireOp",EDGE,"E107");var subQ2=makeQuery(id+"F25.imprint","INTERSECT",VERTEX,{"derivedFrom":[subQ1,subQ0]});Q10=makeQuery(id+"F25.imprint","IMPRINT",FACE,{"disambiguationData":[TD([[makeQuery(id+"F25.imprint","IMPRINT",EDGE,{"disambiguationData":[TD([[subQ2,1.0]])],"derivedFrom":subQ1}),1.0]])]});}
            var Q11;
            {var subQ0=sQuery(id+"F25.wireOp",EDGE,"E111.1.1");Q11=makeQuery(id+"F25.imprint","IMPRINT",FACE,{"disambiguationData":[TD([[makeQuery(id+"F25.imprint","IMPRINT",EDGE,{"derivedFrom":subQ0}),-1.0]])]});}
            extrude(context, id + "F26", {"entities" : qUnion([Q0, Q1, Q2, Q3, Q4, Q5, Q6, Q7, Q8, Q9, Q10, Q11]), "operationType" : NewBodyOperationType.ADD, "depth" : 18 * mm, "offsetDistance" : 25 * mm});
        }
        {
            var Q0;
            Q0=makeQuery(id+"F26.opExtrude","CAP_EDGE",EDGE,{"disambiguationData":[OSD([sQuery(id+"F25.wireOp",EDGE,"E111.2.1")])],"isStart":false});
            var Q1;
            Q1=makeQuery(id+"F26.opExtrude","CAP_EDGE",EDGE,{"disambiguationData":[OSD([sQuery(id+"F25.wireOp",EDGE,"E111.3.1")])],"isStart":false});
            var Q2;
            Q2=makeQuery(id+"F26.opExtrude","CAP_EDGE",EDGE,{"disambiguationData":[OSD([sQuery(id+"F25.wireOp",EDGE,"E111.1.1")])],"isStart":false});
            var Q3;
            Q3=makeQuery(id+"F26.opExtrude","CAP_EDGE",EDGE,{"disambiguationData":[OSD([sQuery(id+"F25.wireOp",EDGE,"E111.4.1")])],"isStart":false});
            var Q4;
            Q4=makeQuery(id+"F26.opExtrude","CAP_EDGE",EDGE,{"disambiguationData":[OSD([sQuery(id+"F25.wireOp",EDGE,"E111.5.1")])],"isStart":false});
            var Q5;
            Q5=makeQuery(id+"F26.opExtrude","CAP_EDGE",EDGE,{"disambiguationData":[OSD([sQuery(id+"F25.wireOp",EDGE,"E108")])],"isStart":false});
            fillet(context, id + "F27", {"entities" : qUnion([Q0, Q1, Q2, Q3, Q4, Q5]), "radius" : 5 * mm, "tangentPropagation" : true, "allowEdgeOverflow" : false});
        }
        {
            var Q0;
            Q0=makeQuery(id+"F24.opRevolve","SWEPT_FACE",FACE,{"disambiguationData":[OSD([sQuery(id+"F23.wireOp",EDGE,"E89.top")])]});
            var sketch = newSketch(context, id + "F28", { "sketchPlane" : qUnion([Q0])});
            skCircle(sketch, "E112", {"center": v(0, 5.91) * mm, "radius": 0.1 * mm});
            skCircle(sketch, "E113.1.0", {"center": v(-1.3, 3.66) * mm, "radius": 0.1 * mm});
            skCircle(sketch, "E113.2.0", {"center": v(1.3, 3.66) * mm, "radius": 0.1 * mm});
            skPoint(sketch, "E113.center", {"position": v(0, 4.41) * mm});
            skSolve(sketch);
        }
        {
            var Q0;
            Q0 = qSketchRegion(id + "F28", true);
            extrude(context, id + "F29", {"entities" : qUnion([Q0]), "operationType" : NewBodyOperationType.ADD, "depth" : 12 * mm, "offsetDistance" : 25 * mm});
        }
        {
            var Q0;
            Q0=makeQuery(id+"F29.opExtrude","CAP_EDGE",EDGE,{"disambiguationData":[OSD([sQuery(id+"F28.wireOp",EDGE,"E113.1.0")])],"isStart":false});
            var Q1;
            Q1=makeQuery(id+"F29.opExtrude","CAP_EDGE",EDGE,{"disambiguationData":[OSD([sQuery(id+"F28.wireOp",EDGE,"E113.2.0")])],"isStart":false});
            var Q2;
            Q2=makeQuery(id+"F29.opExtrude","CAP_EDGE",EDGE,{"disambiguationData":[OSD([sQuery(id+"F28.wireOp",EDGE,"E112")])],"isStart":false});
            fillet(context, id + "F30", {"entities" : qUnion([Q0, Q1, Q2]), "radius" : .1 * mm, "tangentPropagation" : true, "allowEdgeOverflow" : false});
        }
        {
            var Q0;
            Q0=makeQuery(id+"F4.boolean.opBoolean","INTERSECT",EDGE,{"derivedFrom":[makeQuery(id+"F1.opExtrude","SWEPT_FACE",FACE,{"disambiguationData":[OSD([sQuery(id+"F0.wireOp",EDGE,"E18")])]}),makeQuery(id+"F4.opExtrude","SWEPT_FACE",FACE,{"disambiguationData":[OSD([sQuery(id+"F2.wireOp",EDGE,"E28.3.0")])]})]});
            var Q1;
            Q1=makeQuery(id+"F4.boolean.opBoolean","INTERSECT",EDGE,{"derivedFrom":[makeQuery(id+"F1.opExtrude","SWEPT_FACE",FACE,{"disambiguationData":[OSD([sQuery(id+"F0.wireOp",EDGE,"E18")])]}),makeQuery(id+"F4.opExtrude","SWEPT_FACE",FACE,{"disambiguationData":[OSD([sQuery(id+"F2.wireOp",EDGE,"E28.2.0")])]})]});
            var Q2;
            Q2=makeQuery(id+"F4.boolean.opBoolean","INTERSECT",EDGE,{"derivedFrom":[makeQuery(id+"F1.opExtrude","SWEPT_FACE",FACE,{"disambiguationData":[OSD([sQuery(id+"F0.wireOp",EDGE,"E18")])]}),makeQuery(id+"F4.opExtrude","SWEPT_FACE",FACE,{"disambiguationData":[OSD([sQuery(id+"F2.wireOp",EDGE,"E28.4.0")])]})]});
            var Q3;
            Q3=makeQuery(id+"F4.boolean.opBoolean","INTERSECT",EDGE,{"derivedFrom":[makeQuery(id+"F1.opExtrude","SWEPT_FACE",FACE,{"disambiguationData":[OSD([sQuery(id+"F0.wireOp",EDGE,"E18")])]}),makeQuery(id+"F4.opExtrude","SWEPT_FACE",FACE,{"disambiguationData":[OSD([sQuery(id+"F2.wireOp",EDGE,"E28.5.0")])]})]});
            var Q4;
            Q4=makeQuery(id+"F4.boolean.opBoolean","INTERSECT",EDGE,{"derivedFrom":[makeQuery(id+"F1.opExtrude","SWEPT_FACE",FACE,{"disambiguationData":[OSD([sQuery(id+"F0.wireOp",EDGE,"E18")])]}),makeQuery(id+"F4.opExtrude","SWEPT_FACE",FACE,{"disambiguationData":[OSD([sQuery(id+"F2.wireOp",EDGE,"E25")])]})]});
            var Q5;
            Q5=makeQuery(id+"F4.boolean.opBoolean","INTERSECT",EDGE,{"derivedFrom":[makeQuery(id+"F1.opExtrude","SWEPT_FACE",FACE,{"disambiguationData":[OSD([sQuery(id+"F0.wireOp",EDGE,"E18")])]}),makeQuery(id+"F4.opExtrude","SWEPT_FACE",FACE,{"disambiguationData":[OSD([sQuery(id+"F2.wireOp",EDGE,"E28.1.0")])]})]});
            var Q6;
            Q6=makeQuery(id+"F4.boolean.opBoolean","COPY",EDGE,{"derivedFrom":makeQuery(id+"F4.opExtrude","CAP_EDGE",EDGE,{"disambiguationData":[OSD([sQuery(id+"F2.wireOp",EDGE,"E28.3.0")])],"isStart":true})});
            var Q7;
            Q7=makeQuery(id+"F4.boolean.opBoolean","COPY",EDGE,{"derivedFrom":makeQuery(id+"F4.opExtrude","CAP_EDGE",EDGE,{"disambiguationData":[OSD([sQuery(id+"F2.wireOp",EDGE,"E28.4.0")])],"isStart":true})});
            var Q8;
            Q8=makeQuery(id+"F4.boolean.opBoolean","COPY",EDGE,{"derivedFrom":makeQuery(id+"F4.opExtrude","CAP_EDGE",EDGE,{"disambiguationData":[OSD([sQuery(id+"F2.wireOp",EDGE,"E28.5.0")])],"isStart":true})});
            var Q9;
            Q9=makeQuery(id+"F4.boolean.opBoolean","COPY",EDGE,{"derivedFrom":makeQuery(id+"F4.opExtrude","CAP_EDGE",EDGE,{"disambiguationData":[OSD([sQuery(id+"F2.wireOp",EDGE,"E25")])],"isStart":true})});
            var Q10;
            Q10=makeQuery(id+"F4.boolean.opBoolean","COPY",EDGE,{"derivedFrom":makeQuery(id+"F4.opExtrude","CAP_EDGE",EDGE,{"disambiguationData":[OSD([sQuery(id+"F2.wireOp",EDGE,"E28.1.0")])],"isStart":true})});
            var Q11;
            Q11=makeQuery(id+"F4.boolean.opBoolean","COPY",EDGE,{"derivedFrom":makeQuery(id+"F4.opExtrude","CAP_EDGE",EDGE,{"disambiguationData":[OSD([sQuery(id+"F2.wireOp",EDGE,"E28.2.0")])],"isStart":true})});
            var Q12;
            Q12=makeQuery(id+"F5.boolean.opBoolean","COPY",EDGE,{"derivedFrom":makeQuery(id+"F5.opExtrude","CAP_EDGE",EDGE,{"disambiguationData":[OSD([sQuery(id+"F3.wireOp",EDGE,"E38.4.1")])],"isStart":true})});
            var Q13;
            Q13=makeQuery(id+"F5.boolean.opBoolean","COPY",EDGE,{"derivedFrom":makeQuery(id+"F5.opExtrude","CAP_EDGE",EDGE,{"disambiguationData":[OSD([sQuery(id+"F3.wireOp",EDGE,"E38.5.1")])],"isStart":true})});
            var Q14;
            Q14=makeQuery(id+"F5.boolean.opBoolean","COPY",EDGE,{"derivedFrom":makeQuery(id+"F5.opExtrude","CAP_EDGE",EDGE,{"disambiguationData":[OSD([sQuery(id+"F3.wireOp",EDGE,"E35")])],"isStart":true})});
            var Q15;
            Q15=makeQuery(id+"F5.boolean.opBoolean","COPY",EDGE,{"derivedFrom":makeQuery(id+"F5.opExtrude","CAP_EDGE",EDGE,{"disambiguationData":[OSD([sQuery(id+"F3.wireOp",EDGE,"E38.1.1")])],"isStart":true})});
            var Q16;
            Q16=makeQuery(id+"F5.boolean.opBoolean","COPY",EDGE,{"derivedFrom":makeQuery(id+"F5.opExtrude","CAP_EDGE",EDGE,{"disambiguationData":[OSD([sQuery(id+"F3.wireOp",EDGE,"E38.2.1")])],"isStart":true})});
            var Q17;
            Q17=makeQuery(id+"F5.boolean.opBoolean","COPY",EDGE,{"derivedFrom":makeQuery(id+"F5.opExtrude","CAP_EDGE",EDGE,{"disambiguationData":[OSD([sQuery(id+"F3.wireOp",EDGE,"E38.3.1")])],"isStart":true})});
            var Q18;
            Q18=makeQuery(id+"F5.boolean.opBoolean","INTERSECT",EDGE,{"derivedFrom":[makeQuery(id+"F1.opExtrude","SWEPT_FACE",FACE,{"disambiguationData":[OSD([sQuery(id+"F0.wireOp",EDGE,"E19"),sQuery(id+"F0.wireOp",EDGE,"E21.top")])]}),makeQuery(id+"F5.opExtrude","SWEPT_FACE",FACE,{"disambiguationData":[OSD([sQuery(id+"F3.wireOp",EDGE,"E38.5.1")])]})]});
            var Q19;
            Q19=makeQuery(id+"F5.boolean.opBoolean","INTERSECT",EDGE,{"derivedFrom":[makeQuery(id+"F1.opExtrude","SWEPT_FACE",FACE,{"disambiguationData":[OSD([sQuery(id+"F0.wireOp",EDGE,"E19"),sQuery(id+"F0.wireOp",EDGE,"E21.top")])]}),makeQuery(id+"F5.opExtrude","SWEPT_FACE",FACE,{"disambiguationData":[OSD([sQuery(id+"F3.wireOp",EDGE,"E35")])]})]});
            var Q20;
            Q20=makeQuery(id+"F5.boolean.opBoolean","INTERSECT",EDGE,{"derivedFrom":[makeQuery(id+"F1.opExtrude","SWEPT_FACE",FACE,{"disambiguationData":[OSD([sQuery(id+"F0.wireOp",EDGE,"E19"),sQuery(id+"F0.wireOp",EDGE,"E21.top")])]}),makeQuery(id+"F5.opExtrude","SWEPT_FACE",FACE,{"disambiguationData":[OSD([sQuery(id+"F3.wireOp",EDGE,"E38.1.1")])]})]});
            var Q21;
            Q21=makeQuery(id+"F5.boolean.opBoolean","INTERSECT",EDGE,{"derivedFrom":[makeQuery(id+"F1.opExtrude","SWEPT_FACE",FACE,{"disambiguationData":[OSD([sQuery(id+"F0.wireOp",EDGE,"E19"),sQuery(id+"F0.wireOp",EDGE,"E21.top")])]}),makeQuery(id+"F5.opExtrude","SWEPT_FACE",FACE,{"disambiguationData":[OSD([sQuery(id+"F3.wireOp",EDGE,"E38.2.1")])]})]});
            var Q22;
            Q22=makeQuery(id+"F5.boolean.opBoolean","INTERSECT",EDGE,{"derivedFrom":[makeQuery(id+"F1.opExtrude","SWEPT_FACE",FACE,{"disambiguationData":[OSD([sQuery(id+"F0.wireOp",EDGE,"E19"),sQuery(id+"F0.wireOp",EDGE,"E21.top")])]}),makeQuery(id+"F5.opExtrude","SWEPT_FACE",FACE,{"disambiguationData":[OSD([sQuery(id+"F3.wireOp",EDGE,"E38.3.1")])]})]});
            var Q23;
            Q23=makeQuery(id+"F5.boolean.opBoolean","INTERSECT",EDGE,{"derivedFrom":[makeQuery(id+"F1.opExtrude","SWEPT_FACE",FACE,{"disambiguationData":[OSD([sQuery(id+"F0.wireOp",EDGE,"E19"),sQuery(id+"F0.wireOp",EDGE,"E21.top")])]}),makeQuery(id+"F5.opExtrude","SWEPT_FACE",FACE,{"disambiguationData":[OSD([sQuery(id+"F3.wireOp",EDGE,"E38.4.1")])]})]});
            fillet(context, id + "F31", {"entities" : qUnion([Q0, Q1, Q2, Q3, Q4, Q5, Q6, Q7, Q8, Q9, Q10, Q11, Q12, Q13, Q14, Q15, Q16, Q17, Q18, Q19, Q20, Q21, Q22, Q23]), "radius" : .1 * mm, "tangentPropagation" : true, "allowEdgeOverflow" : false});
        }
        {
            var Q0;
            Q0=makeQuery(id+"F21.opRevolve","SWEPT_FACE",FACE,{"disambiguationData":[OSD([sQuery(id+"F15.wireOp",EDGE,"E81.bottom")])]});
            var sketch = newSketch(context, id + "F32", { "sketchPlane" : qUnion([Q0])});
            skCircle(sketch, "E114", {"center": v(2.2, -1.82) * mm, "radius": 0.15 * mm});
            skCircle(sketch, "E115.1.0", {"center": v(2.67, 0.99) * mm, "radius": 0.15 * mm});
            skCircle(sketch, "E115.2.0", {"center": v(0.48, 2.8) * mm, "radius": 0.15 * mm});
            skCircle(sketch, "E115.3.0", {"center": v(-2.2, 1.82) * mm, "radius": 0.15 * mm});
            skCircle(sketch, "E115.4.0", {"center": v(-2.67, -0.99) * mm, "radius": 0.15 * mm});
            skCircle(sketch, "E115.5.0", {"center": v(-0.48, -2.8) * mm, "radius": 0.15 * mm});
            skPoint(sketch, "E115.center", {"position": v(0, 0) * mm});
            skSolve(sketch);
        }
        {
            var Q0;
            Q0 = qSketchRegion(id + "F32", true);
            extrude(context, id + "F33", {"entities" : qUnion([Q0]), "operationType" : NewBodyOperationType.ADD, "oppositeDirection" : true, "depth" : 4.5 * mm, "offsetDistance" : 25 * mm});
        }
        {
            var Q0;
            Q0=makeQuery(id+"F33.boolean.opBoolean","INTERSECT",EDGE,{"derivedFrom":[makeQuery(id+"F21.boolean.opBoolean","MERGE",FACE,{"derivedFrom":[makeQuery(id+"F20.boolean.opBoolean","COPY",FACE,{"derivedFrom":makeQuery(id+"F20.opRevolve","SWEPT_FACE",FACE,{"disambiguationData":[OSD([sQuery(id+"F19.wireOp",EDGE,"E88.right")])]})}),makeQuery(id+"F21.opRevolve","SWEPT_FACE",FACE,{"disambiguationData":[OSD([sQuery(id+"F15.wireOp",EDGE,"E80.right")])]})]}),makeQuery(id+"F33.opExtrude","CAP_FACE",FACE,{"disambiguationData":[OSD([sQuery(id+"F32.wireOp",EDGE,"E114")])],"isStart":false})]});
            var Q1;
            Q1=makeQuery(id+"F33.boolean.opBoolean","INTERSECT",EDGE,{"derivedFrom":[makeQuery(id+"F21.boolean.opBoolean","MERGE",FACE,{"derivedFrom":[makeQuery(id+"F20.boolean.opBoolean","COPY",FACE,{"derivedFrom":makeQuery(id+"F20.opRevolve","SWEPT_FACE",FACE,{"disambiguationData":[OSD([sQuery(id+"F19.wireOp",EDGE,"E88.right")])]})}),makeQuery(id+"F21.opRevolve","SWEPT_FACE",FACE,{"disambiguationData":[OSD([sQuery(id+"F15.wireOp",EDGE,"E80.right")])]})]}),makeQuery(id+"F33.opExtrude","CAP_FACE",FACE,{"disambiguationData":[OSD([sQuery(id+"F32.wireOp",EDGE,"E115.5.0")])],"isStart":false})]});
            var Q2;
            Q2=makeQuery(id+"F33.boolean.opBoolean","INTERSECT",EDGE,{"derivedFrom":[makeQuery(id+"F21.boolean.opBoolean","MERGE",FACE,{"derivedFrom":[makeQuery(id+"F20.boolean.opBoolean","COPY",FACE,{"derivedFrom":makeQuery(id+"F20.opRevolve","SWEPT_FACE",FACE,{"disambiguationData":[OSD([sQuery(id+"F19.wireOp",EDGE,"E88.right")])]})}),makeQuery(id+"F21.opRevolve","SWEPT_FACE",FACE,{"disambiguationData":[OSD([sQuery(id+"F15.wireOp",EDGE,"E80.right")])]})]}),makeQuery(id+"F33.opExtrude","CAP_FACE",FACE,{"disambiguationData":[OSD([sQuery(id+"F32.wireOp",EDGE,"E115.1.0")])],"isStart":false})]});
            var Q3;
            Q3=makeQuery(id+"F33.boolean.opBoolean","INTERSECT",EDGE,{"derivedFrom":[makeQuery(id+"F21.boolean.opBoolean","MERGE",FACE,{"derivedFrom":[makeQuery(id+"F20.boolean.opBoolean","COPY",FACE,{"derivedFrom":makeQuery(id+"F20.opRevolve","SWEPT_FACE",FACE,{"disambiguationData":[OSD([sQuery(id+"F19.wireOp",EDGE,"E88.right")])]})}),makeQuery(id+"F21.opRevolve","SWEPT_FACE",FACE,{"disambiguationData":[OSD([sQuery(id+"F15.wireOp",EDGE,"E80.right")])]})]}),makeQuery(id+"F33.opExtrude","CAP_FACE",FACE,{"disambiguationData":[OSD([sQuery(id+"F32.wireOp",EDGE,"E115.2.0")])],"isStart":false})]});
            var Q4;
            Q4=makeQuery(id+"F33.boolean.opBoolean","INTERSECT",EDGE,{"derivedFrom":[makeQuery(id+"F21.boolean.opBoolean","MERGE",FACE,{"derivedFrom":[makeQuery(id+"F20.boolean.opBoolean","COPY",FACE,{"derivedFrom":makeQuery(id+"F20.opRevolve","SWEPT_FACE",FACE,{"disambiguationData":[OSD([sQuery(id+"F19.wireOp",EDGE,"E88.right")])]})}),makeQuery(id+"F21.opRevolve","SWEPT_FACE",FACE,{"disambiguationData":[OSD([sQuery(id+"F15.wireOp",EDGE,"E80.right")])]})]}),makeQuery(id+"F33.opExtrude","CAP_FACE",FACE,{"disambiguationData":[OSD([sQuery(id+"F32.wireOp",EDGE,"E115.3.0")])],"isStart":false})]});
            var Q5;
            Q5=makeQuery(id+"F33.boolean.opBoolean","INTERSECT",EDGE,{"derivedFrom":[makeQuery(id+"F21.boolean.opBoolean","MERGE",FACE,{"derivedFrom":[makeQuery(id+"F20.boolean.opBoolean","COPY",FACE,{"derivedFrom":makeQuery(id+"F20.opRevolve","SWEPT_FACE",FACE,{"disambiguationData":[OSD([sQuery(id+"F19.wireOp",EDGE,"E88.right")])]})}),makeQuery(id+"F21.opRevolve","SWEPT_FACE",FACE,{"disambiguationData":[OSD([sQuery(id+"F15.wireOp",EDGE,"E80.right")])]})]}),makeQuery(id+"F33.opExtrude","CAP_FACE",FACE,{"disambiguationData":[OSD([sQuery(id+"F32.wireOp",EDGE,"E115.4.0")])],"isStart":false})]});
            fillet(context, id + "F34", {"entities" : qUnion([Q0, Q1, Q2, Q3, Q4, Q5]), "radius" : .2 * mm, "tangentPropagation" : true, "allowEdgeOverflow" : false});
        }
        {
            var Q0;
            Q0=makeQuery(id+"F26.opExtrude","SWEPT_EDGE",EDGE,{"disambiguationData":[OSD([sQuery(id+"F25.wireOp",EDGE,"E111.2.1"),sQuery(id+"F25.wireOp",EDGE,"E111.2.2")])]});
            var Q1;
            Q1=makeQuery(id+"F26.opExtrude","SWEPT_EDGE",EDGE,{"disambiguationData":[OSD([sQuery(id+"F25.wireOp",EDGE,"E111.2.0"),sQuery(id+"F25.wireOp",EDGE,"E111.2.1")])]});
            var Q2;
            Q2=makeQuery(id+"F26.opExtrude","SWEPT_EDGE",EDGE,{"disambiguationData":[OSD([sQuery(id+"F25.wireOp",EDGE,"E111.1.0"),sQuery(id+"F25.wireOp",EDGE,"E111.1.1")])]});
            var Q3;
            Q3=makeQuery(id+"F26.opExtrude","SWEPT_EDGE",EDGE,{"disambiguationData":[OSD([sQuery(id+"F25.wireOp",EDGE,"E111.1.1"),sQuery(id+"F25.wireOp",EDGE,"E111.1.2")])]});
            var Q4;
            Q4=makeQuery(id+"F26.opExtrude","SWEPT_EDGE",EDGE,{"disambiguationData":[OSD([sQuery(id+"F25.wireOp",EDGE,"E108"),sQuery(id+"F25.wireOp",EDGE,"E109")])]});
            var Q5;
            Q5=makeQuery(id+"F26.opExtrude","SWEPT_EDGE",EDGE,{"disambiguationData":[OSD([sQuery(id+"F25.wireOp",EDGE,"E108"),sQuery(id+"F25.wireOp",EDGE,"E110")])]});
            var Q6;
            Q6=makeQuery(id+"F26.opExtrude","SWEPT_EDGE",EDGE,{"disambiguationData":[OSD([sQuery(id+"F25.wireOp",EDGE,"E111.5.0"),sQuery(id+"F25.wireOp",EDGE,"E111.5.1")])]});
            var Q7;
            Q7=makeQuery(id+"F26.opExtrude","SWEPT_EDGE",EDGE,{"disambiguationData":[OSD([sQuery(id+"F25.wireOp",EDGE,"E111.5.1"),sQuery(id+"F25.wireOp",EDGE,"E111.5.2")])]});
            var Q8;
            Q8=makeQuery(id+"F26.opExtrude","SWEPT_EDGE",EDGE,{"disambiguationData":[OSD([sQuery(id+"F25.wireOp",EDGE,"E111.4.0"),sQuery(id+"F25.wireOp",EDGE,"E111.4.1")])]});
            var Q9;
            Q9=makeQuery(id+"F26.opExtrude","SWEPT_EDGE",EDGE,{"disambiguationData":[OSD([sQuery(id+"F25.wireOp",EDGE,"E111.4.1"),sQuery(id+"F25.wireOp",EDGE,"E111.4.2")])]});
            var Q10;
            Q10=makeQuery(id+"F26.opExtrude","SWEPT_EDGE",EDGE,{"disambiguationData":[OSD([sQuery(id+"F25.wireOp",EDGE,"E111.3.0"),sQuery(id+"F25.wireOp",EDGE,"E111.3.1")])]});
            var Q11;
            Q11=makeQuery(id+"F26.opExtrude","SWEPT_EDGE",EDGE,{"disambiguationData":[OSD([sQuery(id+"F25.wireOp",EDGE,"E111.3.1"),sQuery(id+"F25.wireOp",EDGE,"E111.3.2")])]});
            fillet(context, id + "F35", {"entities" : qUnion([Q0, Q1, Q2, Q3, Q4, Q5, Q6, Q7, Q8, Q9, Q10, Q11]), "radius" : .1 * mm, "tangentPropagation" : true, "allowEdgeOverflow" : false});
        }
        {
            var Q0;
            {var subQ0=sQuery(id+"F23.wireOp",EDGE,"E96");Q0=makeQuery(id+"F23.imprint","IMPRINT",FACE,{"disambiguationData":[TD([[makeQuery(id+"F23.imprint","IMPRINT",EDGE,{"derivedFrom":subQ0}),1.0]])]});}
            var Q1;
            Q1=sQuery(id+"F23.wireOp",EDGE,"E101.trimOffspring");
            revolve(context, id + "F36", {"surfaceOperationType" : NewSurfaceOperationType.NEW, "entities" : qUnion([Q0]), "axis" : qUnion([Q1]), "revolveType" : RevolveType.FULL});
        }
    });
